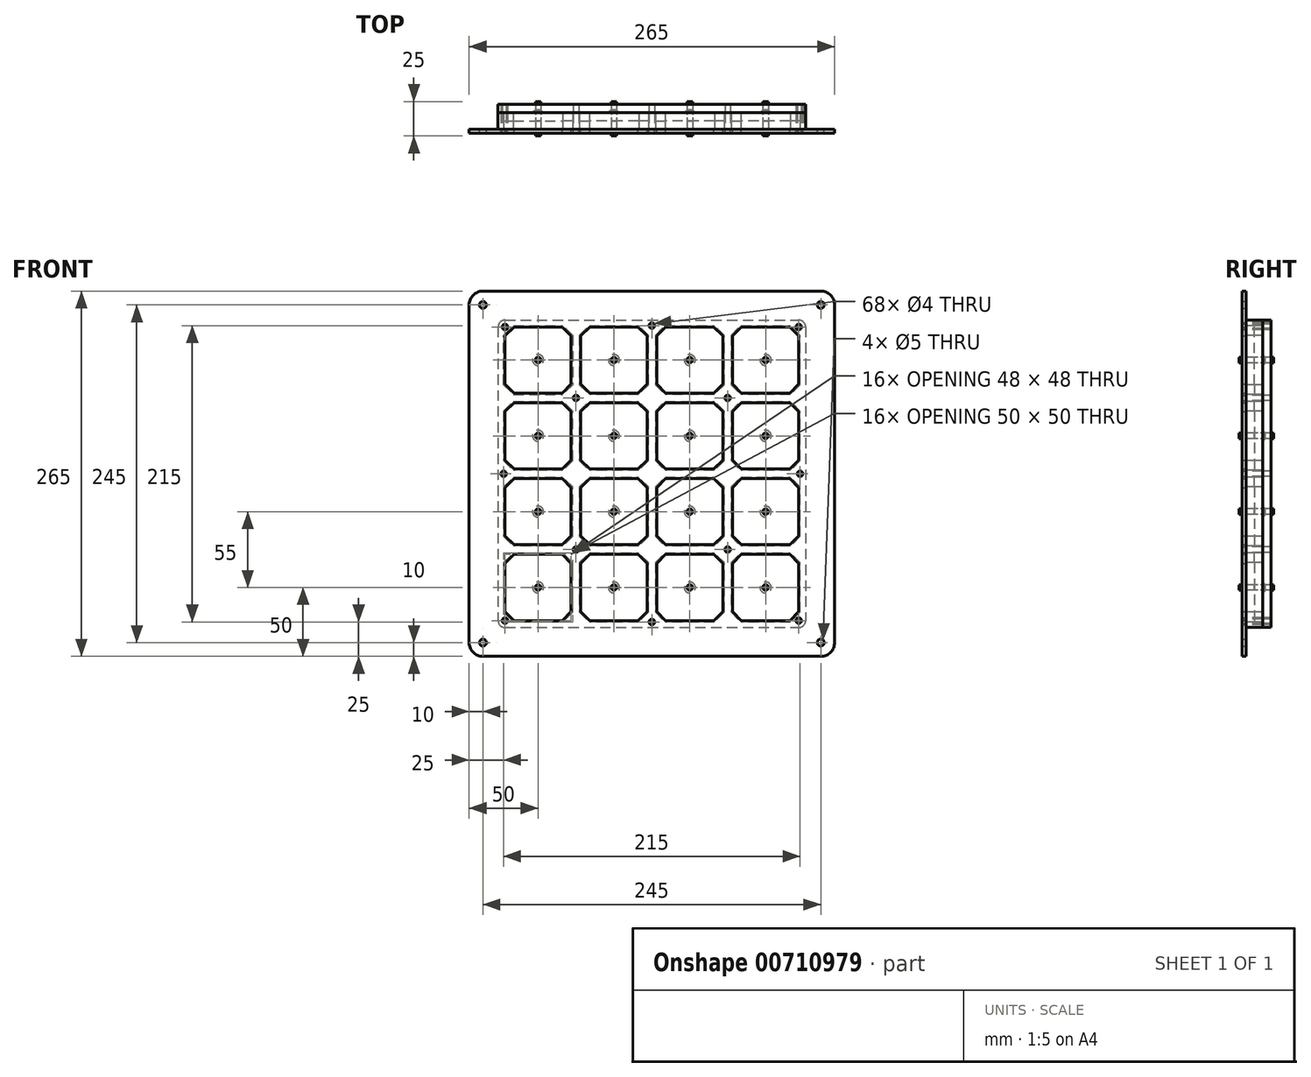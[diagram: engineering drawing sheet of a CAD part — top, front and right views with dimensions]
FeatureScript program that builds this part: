
annotation { "Feature Type Name" : "Feature", "Feature Type Description" : "" }
export const myFeature = defineFeature(function(context is Context, id is Id, definition is map)
    precondition{}
    {
        {
            var Q0;
            Q0=qCreatedBy(makeId("Front.planeOp"),FACE);
            var sketch = newSketch(context, id + "F0", { "sketchPlane" : qUnion([Q0])});
            skLineSegment(sketch, "E0.bottom", {"start": v(-106.5, 111.5) * mm, "end": v(106.5, 111.5) * mm});
            skLineSegment(sketch, "E0.top", {"start": v(-106.5, -111.5) * mm, "end": v(106.5, -111.5) * mm});
            skLineSegment(sketch, "E0.left", {"start": v(-111.5, 106.5) * mm, "end": v(-111.5, -106.5) * mm});
            skLineSegment(sketch, "E0.right", {"start": v(111.5, 106.5) * mm, "end": v(111.5, -106.5) * mm});
            skLineSegment(sketch, "E1", {"start": v(-82.5, 107.5) * mm, "end": v(-82.5, 57.5) * mm, "construction": true});
            skLineSegment(sketch, "E2", {"start": v(-107.5, 82.5) * mm, "end": v(-82.5, 82.5) * mm, "construction": true});
            skLineSegment(sketch, "E3", {"start": v(-82.5, 82.5) * mm, "end": v(-57.5, 82.5) * mm, "construction": true});
            skLineSegment(sketch, "E4", {"start": v(-107.5, 82.5) * mm, "end": v(-107.5, 100.43) * mm});
            skLineSegment(sketch, "E5", {"start": v(-107.5, 100.43) * mm, "end": v(-100.43, 107.5) * mm});
            skLineSegment(sketch, "E6", {"start": v(-100.43, 107.5) * mm, "end": v(-82.5, 107.5) * mm});
            skLineSegment(sketch, "E7.MirrorCS", {"start": v(-57.5, 82.5) * mm, "end": v(-57.5, 100.43) * mm});
            skLineSegment(sketch, "E8.MirrorCS", {"start": v(-57.5, 100.43) * mm, "end": v(-64.57, 107.5) * mm});
            skLineSegment(sketch, "E9.MirrorCS", {"start": v(-64.57, 107.5) * mm, "end": v(-82.5, 107.5) * mm});
            skLineSegment(sketch, "E10.MirrorCS", {"start": v(-57.5, 82.5) * mm, "end": v(-57.5, 64.57) * mm});
            skLineSegment(sketch, "E11.MirrorCS", {"start": v(-57.5, 64.57) * mm, "end": v(-64.57, 57.5) * mm});
            skLineSegment(sketch, "E12.MirrorCS", {"start": v(-64.57, 57.5) * mm, "end": v(-82.5, 57.5) * mm});
            skLineSegment(sketch, "E13.MirrorCS", {"start": v(-100.43, 57.5) * mm, "end": v(-82.5, 57.5) * mm});
            skLineSegment(sketch, "E14.MirrorCS", {"start": v(-107.5, 82.5) * mm, "end": v(-107.5, 64.57) * mm});
            skLineSegment(sketch, "E15.MirrorCS", {"start": v(-107.5, 64.57) * mm, "end": v(-100.43, 57.5) * mm});
            skPoint(sketch, "E16.visualSharp", {"position": v(-111.5, 111.5) * mm});
            skArc(sketch, "E16.filletArc", {"start": v(-106.5, 111.5) * mm, "mid": v(-110.04, 110.04) * mm, "end": v(-111.5, 106.5) * mm});
            skPoint(sketch, "E17.visualSharp", {"position": v(111.5, 111.5) * mm});
            skArc(sketch, "E17.filletArc", {"start": v(111.5, 106.5) * mm, "mid": v(110.04, 110.04) * mm, "end": v(106.5, 111.5) * mm});
            skPoint(sketch, "E18.visualSharp", {"position": v(111.5, -111.5) * mm});
            skArc(sketch, "E18.filletArc", {"start": v(106.5, -111.5) * mm, "mid": v(110.04, -110.04) * mm, "end": v(111.5, -106.5) * mm});
            skPoint(sketch, "E19.visualSharp", {"position": v(-111.5, -111.5) * mm});
            skArc(sketch, "E19.filletArc", {"start": v(-111.5, -106.5) * mm, "mid": v(-110.04, -110.04) * mm, "end": v(-106.5, -111.5) * mm});
            skCircle(sketch, "E20", {"center": v(-82.5, 82.5) * mm, "radius": 2 * mm});
            skLineSegment(sketch, "E21.0.1.0", {"start": v(-57.5, 45.43) * mm, "end": v(-64.57, 52.5) * mm});
            skLineSegment(sketch, "E21.0.1.1", {"start": v(-107.5, 27.5) * mm, "end": v(-82.5, 27.5) * mm, "construction": true});
            skLineSegment(sketch, "E21.0.1.2", {"start": v(-100.43, 52.5) * mm, "end": v(-82.5, 52.5) * mm});
            skLineSegment(sketch, "E21.0.1.3", {"start": v(-107.5, 45.43) * mm, "end": v(-100.43, 52.5) * mm});
            skLineSegment(sketch, "E21.0.1.4", {"start": v(-107.5, 27.5) * mm, "end": v(-107.5, 45.43) * mm});
            skLineSegment(sketch, "E21.0.1.5", {"start": v(-64.57, 52.5) * mm, "end": v(-82.5, 52.5) * mm});
            skLineSegment(sketch, "E21.0.1.6", {"start": v(-107.5, 9.57) * mm, "end": v(-100.43, 2.5) * mm});
            skLineSegment(sketch, "E21.0.1.7", {"start": v(-64.57, 2.5) * mm, "end": v(-82.5, 2.5) * mm});
            skCircle(sketch, "E21.0.1.8", {"center": v(-82.5, 27.5) * mm, "radius": 2 * mm});
            skLineSegment(sketch, "E21.0.1.9", {"start": v(-57.5, 9.57) * mm, "end": v(-64.57, 2.5) * mm});
            skLineSegment(sketch, "E21.0.1.10", {"start": v(-100.43, 2.5) * mm, "end": v(-82.5, 2.5) * mm});
            skLineSegment(sketch, "E21.0.1.11", {"start": v(-82.5, 27.5) * mm, "end": v(-57.5, 27.5) * mm, "construction": true});
            skLineSegment(sketch, "E21.0.1.12", {"start": v(-57.5, 27.5) * mm, "end": v(-57.5, 45.43) * mm});
            skLineSegment(sketch, "E21.0.1.13", {"start": v(-57.5, 27.5) * mm, "end": v(-57.5, 9.57) * mm});
            skLineSegment(sketch, "E21.0.1.14", {"start": v(-107.5, 27.5) * mm, "end": v(-107.5, 9.57) * mm});
            skLineSegment(sketch, "E21.0.1.15", {"start": v(-82.5, 52.5) * mm, "end": v(-82.5, 2.5) * mm, "construction": true});
            skLineSegment(sketch, "E21.0.1.16", {"start": v(-57.5, 27.5) * mm, "end": v(-57.5, 45.43) * mm});
            skLineSegment(sketch, "E21.0.1.17", {"start": v(-57.5, 45.43) * mm, "end": v(-64.57, 52.5) * mm});
            skLineSegment(sketch, "E21.0.1.18", {"start": v(-57.5, 27.5) * mm, "end": v(-57.5, 45.43) * mm});
            skLineSegment(sketch, "E21.0.2.0", {"start": v(-57.5, -9.57) * mm, "end": v(-64.57, -2.5) * mm});
            skLineSegment(sketch, "E21.0.2.1", {"start": v(-107.5, -27.5) * mm, "end": v(-82.5, -27.5) * mm, "construction": true});
            skLineSegment(sketch, "E21.0.2.2", {"start": v(-100.43, -2.5) * mm, "end": v(-82.5, -2.5) * mm});
            skLineSegment(sketch, "E21.0.2.3", {"start": v(-107.5, -9.57) * mm, "end": v(-100.43, -2.5) * mm});
            skLineSegment(sketch, "E21.0.2.4", {"start": v(-107.5, -27.5) * mm, "end": v(-107.5, -9.57) * mm});
            skLineSegment(sketch, "E21.0.2.5", {"start": v(-64.57, -2.5) * mm, "end": v(-82.5, -2.5) * mm});
            skLineSegment(sketch, "E21.0.2.6", {"start": v(-107.5, -45.43) * mm, "end": v(-100.43, -52.5) * mm});
            skLineSegment(sketch, "E21.0.2.7", {"start": v(-64.57, -52.5) * mm, "end": v(-82.5, -52.5) * mm});
            skCircle(sketch, "E21.0.2.8", {"center": v(-82.5, -27.5) * mm, "radius": 2 * mm});
            skLineSegment(sketch, "E21.0.2.9", {"start": v(-57.5, -45.43) * mm, "end": v(-64.57, -52.5) * mm});
            skLineSegment(sketch, "E21.0.2.10", {"start": v(-100.43, -52.5) * mm, "end": v(-82.5, -52.5) * mm});
            skLineSegment(sketch, "E21.0.2.11", {"start": v(-82.5, -27.5) * mm, "end": v(-57.5, -27.5) * mm, "construction": true});
            skLineSegment(sketch, "E21.0.2.12", {"start": v(-57.5, -27.5) * mm, "end": v(-57.5, -9.57) * mm});
            skLineSegment(sketch, "E21.0.2.13", {"start": v(-57.5, -27.5) * mm, "end": v(-57.5, -45.43) * mm});
            skLineSegment(sketch, "E21.0.2.14", {"start": v(-107.5, -27.5) * mm, "end": v(-107.5, -45.43) * mm});
            skLineSegment(sketch, "E21.0.2.15", {"start": v(-82.5, -2.5) * mm, "end": v(-82.5, -52.5) * mm, "construction": true});
            skLineSegment(sketch, "E21.0.2.16", {"start": v(-57.5, -27.5) * mm, "end": v(-57.5, -9.57) * mm});
            skLineSegment(sketch, "E21.0.2.17", {"start": v(-57.5, -9.57) * mm, "end": v(-64.57, -2.5) * mm});
            skLineSegment(sketch, "E21.0.2.18", {"start": v(-57.5, -27.5) * mm, "end": v(-57.5, -9.57) * mm});
            skLineSegment(sketch, "E21.0.3.0", {"start": v(-57.5, -64.57) * mm, "end": v(-64.57, -57.5) * mm});
            skLineSegment(sketch, "E21.0.3.1", {"start": v(-107.5, -82.5) * mm, "end": v(-82.5, -82.5) * mm, "construction": true});
            skLineSegment(sketch, "E21.0.3.2", {"start": v(-100.43, -57.5) * mm, "end": v(-82.5, -57.5) * mm});
            skLineSegment(sketch, "E21.0.3.3", {"start": v(-107.5, -64.57) * mm, "end": v(-100.43, -57.5) * mm});
            skLineSegment(sketch, "E21.0.3.4", {"start": v(-107.5, -82.5) * mm, "end": v(-107.5, -64.57) * mm});
            skLineSegment(sketch, "E21.0.3.5", {"start": v(-64.57, -57.5) * mm, "end": v(-82.5, -57.5) * mm});
            skLineSegment(sketch, "E21.0.3.6", {"start": v(-107.5, -100.43) * mm, "end": v(-100.43, -107.5) * mm});
            skLineSegment(sketch, "E21.0.3.7", {"start": v(-64.57, -107.5) * mm, "end": v(-82.5, -107.5) * mm});
            skCircle(sketch, "E21.0.3.8", {"center": v(-82.5, -82.5) * mm, "radius": 2 * mm});
            skLineSegment(sketch, "E21.0.3.9", {"start": v(-57.5, -100.43) * mm, "end": v(-64.57, -107.5) * mm});
            skLineSegment(sketch, "E21.0.3.10", {"start": v(-100.43, -107.5) * mm, "end": v(-82.5, -107.5) * mm});
            skLineSegment(sketch, "E21.0.3.11", {"start": v(-82.5, -82.5) * mm, "end": v(-57.5, -82.5) * mm, "construction": true});
            skLineSegment(sketch, "E21.0.3.12", {"start": v(-57.5, -82.5) * mm, "end": v(-57.5, -64.57) * mm});
            skLineSegment(sketch, "E21.0.3.13", {"start": v(-57.5, -82.5) * mm, "end": v(-57.5, -100.43) * mm});
            skLineSegment(sketch, "E21.0.3.14", {"start": v(-107.5, -82.5) * mm, "end": v(-107.5, -100.43) * mm});
            skLineSegment(sketch, "E21.0.3.15", {"start": v(-82.5, -57.5) * mm, "end": v(-82.5, -107.5) * mm, "construction": true});
            skLineSegment(sketch, "E21.0.3.16", {"start": v(-57.5, -82.5) * mm, "end": v(-57.5, -64.57) * mm});
            skLineSegment(sketch, "E21.0.3.17", {"start": v(-57.5, -64.57) * mm, "end": v(-64.57, -57.5) * mm});
            skLineSegment(sketch, "E21.0.3.18", {"start": v(-57.5, -82.5) * mm, "end": v(-57.5, -64.57) * mm});
            skLineSegment(sketch, "E21.1.0.0", {"start": v(-2.5, 100.43) * mm, "end": v(-9.57, 107.5) * mm});
            skLineSegment(sketch, "E21.1.0.1", {"start": v(-52.5, 82.5) * mm, "end": v(-27.5, 82.5) * mm, "construction": true});
            skLineSegment(sketch, "E21.1.0.2", {"start": v(-45.43, 107.5) * mm, "end": v(-27.5, 107.5) * mm});
            skLineSegment(sketch, "E21.1.0.3", {"start": v(-52.5, 100.43) * mm, "end": v(-45.43, 107.5) * mm});
            skLineSegment(sketch, "E21.1.0.4", {"start": v(-52.5, 82.5) * mm, "end": v(-52.5, 100.43) * mm});
            skLineSegment(sketch, "E21.1.0.5", {"start": v(-9.57, 107.5) * mm, "end": v(-27.5, 107.5) * mm});
            skLineSegment(sketch, "E21.1.0.6", {"start": v(-52.5, 64.57) * mm, "end": v(-45.43, 57.5) * mm});
            skLineSegment(sketch, "E21.1.0.7", {"start": v(-9.57, 57.5) * mm, "end": v(-27.5, 57.5) * mm});
            skCircle(sketch, "E21.1.0.8", {"center": v(-27.5, 82.5) * mm, "radius": 2 * mm});
            skLineSegment(sketch, "E21.1.0.9", {"start": v(-2.5, 64.57) * mm, "end": v(-9.57, 57.5) * mm});
            skLineSegment(sketch, "E21.1.0.10", {"start": v(-45.43, 57.5) * mm, "end": v(-27.5, 57.5) * mm});
            skLineSegment(sketch, "E21.1.0.11", {"start": v(-27.5, 82.5) * mm, "end": v(-2.5, 82.5) * mm, "construction": true});
            skLineSegment(sketch, "E21.1.0.12", {"start": v(-2.5, 82.5) * mm, "end": v(-2.5, 100.43) * mm});
            skLineSegment(sketch, "E21.1.0.13", {"start": v(-2.5, 82.5) * mm, "end": v(-2.5, 64.57) * mm});
            skLineSegment(sketch, "E21.1.0.14", {"start": v(-52.5, 82.5) * mm, "end": v(-52.5, 64.57) * mm});
            skLineSegment(sketch, "E21.1.0.15", {"start": v(-27.5, 107.5) * mm, "end": v(-27.5, 57.5) * mm, "construction": true});
            skLineSegment(sketch, "E21.1.0.16", {"start": v(-2.5, 82.5) * mm, "end": v(-2.5, 100.43) * mm});
            skLineSegment(sketch, "E21.1.0.17", {"start": v(-2.5, 100.43) * mm, "end": v(-9.57, 107.5) * mm});
            skLineSegment(sketch, "E21.1.0.18", {"start": v(-2.5, 82.5) * mm, "end": v(-2.5, 100.43) * mm});
            skLineSegment(sketch, "E21.1.1.0", {"start": v(-2.5, 45.43) * mm, "end": v(-9.57, 52.5) * mm});
            skLineSegment(sketch, "E21.1.1.1", {"start": v(-52.5, 27.5) * mm, "end": v(-27.5, 27.5) * mm, "construction": true});
            skLineSegment(sketch, "E21.1.1.2", {"start": v(-45.43, 52.5) * mm, "end": v(-27.5, 52.5) * mm});
            skLineSegment(sketch, "E21.1.1.3", {"start": v(-52.5, 45.43) * mm, "end": v(-45.43, 52.5) * mm});
            skLineSegment(sketch, "E21.1.1.4", {"start": v(-52.5, 27.5) * mm, "end": v(-52.5, 45.43) * mm});
            skLineSegment(sketch, "E21.1.1.5", {"start": v(-9.57, 52.5) * mm, "end": v(-27.5, 52.5) * mm});
            skLineSegment(sketch, "E21.1.1.6", {"start": v(-52.5, 9.57) * mm, "end": v(-45.43, 2.5) * mm});
            skLineSegment(sketch, "E21.1.1.7", {"start": v(-9.57, 2.5) * mm, "end": v(-27.5, 2.5) * mm});
            skCircle(sketch, "E21.1.1.8", {"center": v(-27.5, 27.5) * mm, "radius": 2 * mm});
            skLineSegment(sketch, "E21.1.1.9", {"start": v(-2.5, 9.57) * mm, "end": v(-9.57, 2.5) * mm});
            skLineSegment(sketch, "E21.1.1.10", {"start": v(-45.43, 2.5) * mm, "end": v(-27.5, 2.5) * mm});
            skLineSegment(sketch, "E21.1.1.11", {"start": v(-27.5, 27.5) * mm, "end": v(-2.5, 27.5) * mm, "construction": true});
            skLineSegment(sketch, "E21.1.1.12", {"start": v(-2.5, 27.5) * mm, "end": v(-2.5, 45.43) * mm});
            skLineSegment(sketch, "E21.1.1.13", {"start": v(-2.5, 27.5) * mm, "end": v(-2.5, 9.57) * mm});
            skLineSegment(sketch, "E21.1.1.14", {"start": v(-52.5, 27.5) * mm, "end": v(-52.5, 9.57) * mm});
            skLineSegment(sketch, "E21.1.1.15", {"start": v(-27.5, 52.5) * mm, "end": v(-27.5, 2.5) * mm, "construction": true});
            skLineSegment(sketch, "E21.1.1.16", {"start": v(-2.5, 27.5) * mm, "end": v(-2.5, 45.43) * mm});
            skLineSegment(sketch, "E21.1.1.17", {"start": v(-2.5, 45.43) * mm, "end": v(-9.57, 52.5) * mm});
            skLineSegment(sketch, "E21.1.1.18", {"start": v(-2.5, 27.5) * mm, "end": v(-2.5, 45.43) * mm});
            skLineSegment(sketch, "E21.1.2.0", {"start": v(-2.5, -9.57) * mm, "end": v(-9.57, -2.5) * mm});
            skLineSegment(sketch, "E21.1.2.1", {"start": v(-52.5, -27.5) * mm, "end": v(-27.5, -27.5) * mm, "construction": true});
            skLineSegment(sketch, "E21.1.2.2", {"start": v(-45.43, -2.5) * mm, "end": v(-27.5, -2.5) * mm});
            skLineSegment(sketch, "E21.1.2.3", {"start": v(-52.5, -9.57) * mm, "end": v(-45.43, -2.5) * mm});
            skLineSegment(sketch, "E21.1.2.4", {"start": v(-52.5, -27.5) * mm, "end": v(-52.5, -9.57) * mm});
            skLineSegment(sketch, "E21.1.2.5", {"start": v(-9.57, -2.5) * mm, "end": v(-27.5, -2.5) * mm});
            skLineSegment(sketch, "E21.1.2.6", {"start": v(-52.5, -45.43) * mm, "end": v(-45.43, -52.5) * mm});
            skLineSegment(sketch, "E21.1.2.7", {"start": v(-9.57, -52.5) * mm, "end": v(-27.5, -52.5) * mm});
            skCircle(sketch, "E21.1.2.8", {"center": v(-27.5, -27.5) * mm, "radius": 2 * mm});
            skLineSegment(sketch, "E21.1.2.9", {"start": v(-2.5, -45.43) * mm, "end": v(-9.57, -52.5) * mm});
            skLineSegment(sketch, "E21.1.2.10", {"start": v(-45.43, -52.5) * mm, "end": v(-27.5, -52.5) * mm});
            skLineSegment(sketch, "E21.1.2.11", {"start": v(-27.5, -27.5) * mm, "end": v(-2.5, -27.5) * mm, "construction": true});
            skLineSegment(sketch, "E21.1.2.12", {"start": v(-2.5, -27.5) * mm, "end": v(-2.5, -9.57) * mm});
            skLineSegment(sketch, "E21.1.2.13", {"start": v(-2.5, -27.5) * mm, "end": v(-2.5, -45.43) * mm});
            skLineSegment(sketch, "E21.1.2.14", {"start": v(-52.5, -27.5) * mm, "end": v(-52.5, -45.43) * mm});
            skLineSegment(sketch, "E21.1.2.15", {"start": v(-27.5, -2.5) * mm, "end": v(-27.5, -52.5) * mm, "construction": true});
            skLineSegment(sketch, "E21.1.2.16", {"start": v(-2.5, -27.5) * mm, "end": v(-2.5, -9.57) * mm});
            skLineSegment(sketch, "E21.1.2.17", {"start": v(-2.5, -9.57) * mm, "end": v(-9.57, -2.5) * mm});
            skLineSegment(sketch, "E21.1.2.18", {"start": v(-2.5, -27.5) * mm, "end": v(-2.5, -9.57) * mm});
            skLineSegment(sketch, "E21.1.3.0", {"start": v(-2.5, -64.57) * mm, "end": v(-9.57, -57.5) * mm});
            skLineSegment(sketch, "E21.1.3.1", {"start": v(-52.5, -82.5) * mm, "end": v(-27.5, -82.5) * mm, "construction": true});
            skLineSegment(sketch, "E21.1.3.2", {"start": v(-45.43, -57.5) * mm, "end": v(-27.5, -57.5) * mm});
            skLineSegment(sketch, "E21.1.3.3", {"start": v(-52.5, -64.57) * mm, "end": v(-45.43, -57.5) * mm});
            skLineSegment(sketch, "E21.1.3.4", {"start": v(-52.5, -82.5) * mm, "end": v(-52.5, -64.57) * mm});
            skLineSegment(sketch, "E21.1.3.5", {"start": v(-9.57, -57.5) * mm, "end": v(-27.5, -57.5) * mm});
            skLineSegment(sketch, "E21.1.3.6", {"start": v(-52.5, -100.43) * mm, "end": v(-45.43, -107.5) * mm});
            skLineSegment(sketch, "E21.1.3.7", {"start": v(-9.57, -107.5) * mm, "end": v(-27.5, -107.5) * mm});
            skCircle(sketch, "E21.1.3.8", {"center": v(-27.5, -82.5) * mm, "radius": 2 * mm});
            skLineSegment(sketch, "E21.1.3.9", {"start": v(-2.5, -100.43) * mm, "end": v(-9.57, -107.5) * mm});
            skLineSegment(sketch, "E21.1.3.10", {"start": v(-45.43, -107.5) * mm, "end": v(-27.5, -107.5) * mm});
            skLineSegment(sketch, "E21.1.3.11", {"start": v(-27.5, -82.5) * mm, "end": v(-2.5, -82.5) * mm, "construction": true});
            skLineSegment(sketch, "E21.1.3.12", {"start": v(-2.5, -82.5) * mm, "end": v(-2.5, -64.57) * mm});
            skLineSegment(sketch, "E21.1.3.13", {"start": v(-2.5, -82.5) * mm, "end": v(-2.5, -100.43) * mm});
            skLineSegment(sketch, "E21.1.3.14", {"start": v(-52.5, -82.5) * mm, "end": v(-52.5, -100.43) * mm});
            skLineSegment(sketch, "E21.1.3.15", {"start": v(-27.5, -57.5) * mm, "end": v(-27.5, -107.5) * mm, "construction": true});
            skLineSegment(sketch, "E21.1.3.16", {"start": v(-2.5, -82.5) * mm, "end": v(-2.5, -64.57) * mm});
            skLineSegment(sketch, "E21.1.3.17", {"start": v(-2.5, -64.57) * mm, "end": v(-9.57, -57.5) * mm});
            skLineSegment(sketch, "E21.1.3.18", {"start": v(-2.5, -82.5) * mm, "end": v(-2.5, -64.57) * mm});
            skLineSegment(sketch, "E21.2.0.0", {"start": v(52.5, 100.43) * mm, "end": v(45.43, 107.5) * mm});
            skLineSegment(sketch, "E21.2.0.1", {"start": v(2.5, 82.5) * mm, "end": v(27.5, 82.5) * mm, "construction": true});
            skLineSegment(sketch, "E21.2.0.2", {"start": v(9.57, 107.5) * mm, "end": v(27.5, 107.5) * mm});
            skLineSegment(sketch, "E21.2.0.3", {"start": v(2.5, 100.43) * mm, "end": v(9.57, 107.5) * mm});
            skLineSegment(sketch, "E21.2.0.4", {"start": v(2.5, 82.5) * mm, "end": v(2.5, 100.43) * mm});
            skLineSegment(sketch, "E21.2.0.5", {"start": v(45.43, 107.5) * mm, "end": v(27.5, 107.5) * mm});
            skLineSegment(sketch, "E21.2.0.6", {"start": v(2.5, 64.57) * mm, "end": v(9.57, 57.5) * mm});
            skLineSegment(sketch, "E21.2.0.7", {"start": v(45.43, 57.5) * mm, "end": v(27.5, 57.5) * mm});
            skCircle(sketch, "E21.2.0.8", {"center": v(27.5, 82.5) * mm, "radius": 2 * mm});
            skLineSegment(sketch, "E21.2.0.9", {"start": v(52.5, 64.57) * mm, "end": v(45.43, 57.5) * mm});
            skLineSegment(sketch, "E21.2.0.10", {"start": v(9.57, 57.5) * mm, "end": v(27.5, 57.5) * mm});
            skLineSegment(sketch, "E21.2.0.11", {"start": v(27.5, 82.5) * mm, "end": v(52.5, 82.5) * mm, "construction": true});
            skLineSegment(sketch, "E21.2.0.12", {"start": v(52.5, 82.5) * mm, "end": v(52.5, 100.43) * mm});
            skLineSegment(sketch, "E21.2.0.13", {"start": v(52.5, 82.5) * mm, "end": v(52.5, 64.57) * mm});
            skLineSegment(sketch, "E21.2.0.14", {"start": v(2.5, 82.5) * mm, "end": v(2.5, 64.57) * mm});
            skLineSegment(sketch, "E21.2.0.15", {"start": v(27.5, 107.5) * mm, "end": v(27.5, 57.5) * mm, "construction": true});
            skLineSegment(sketch, "E21.2.0.16", {"start": v(52.5, 82.5) * mm, "end": v(52.5, 100.43) * mm});
            skLineSegment(sketch, "E21.2.0.17", {"start": v(52.5, 100.43) * mm, "end": v(45.43, 107.5) * mm});
            skLineSegment(sketch, "E21.2.0.18", {"start": v(52.5, 82.5) * mm, "end": v(52.5, 100.43) * mm});
            skLineSegment(sketch, "E21.2.1.0", {"start": v(52.5, 45.43) * mm, "end": v(45.43, 52.5) * mm});
            skLineSegment(sketch, "E21.2.1.1", {"start": v(2.5, 27.5) * mm, "end": v(27.5, 27.5) * mm, "construction": true});
            skLineSegment(sketch, "E21.2.1.2", {"start": v(9.57, 52.5) * mm, "end": v(27.5, 52.5) * mm});
            skLineSegment(sketch, "E21.2.1.3", {"start": v(2.5, 45.43) * mm, "end": v(9.57, 52.5) * mm});
            skLineSegment(sketch, "E21.2.1.4", {"start": v(2.5, 27.5) * mm, "end": v(2.5, 45.43) * mm});
            skLineSegment(sketch, "E21.2.1.5", {"start": v(45.43, 52.5) * mm, "end": v(27.5, 52.5) * mm});
            skLineSegment(sketch, "E21.2.1.6", {"start": v(2.5, 9.57) * mm, "end": v(9.57, 2.5) * mm});
            skLineSegment(sketch, "E21.2.1.7", {"start": v(45.43, 2.5) * mm, "end": v(27.5, 2.5) * mm});
            skCircle(sketch, "E21.2.1.8", {"center": v(27.5, 27.5) * mm, "radius": 2 * mm});
            skLineSegment(sketch, "E21.2.1.9", {"start": v(52.5, 9.57) * mm, "end": v(45.43, 2.5) * mm});
            skLineSegment(sketch, "E21.2.1.10", {"start": v(9.57, 2.5) * mm, "end": v(27.5, 2.5) * mm});
            skLineSegment(sketch, "E21.2.1.11", {"start": v(27.5, 27.5) * mm, "end": v(52.5, 27.5) * mm, "construction": true});
            skLineSegment(sketch, "E21.2.1.12", {"start": v(52.5, 27.5) * mm, "end": v(52.5, 45.43) * mm});
            skLineSegment(sketch, "E21.2.1.13", {"start": v(52.5, 27.5) * mm, "end": v(52.5, 9.57) * mm});
            skLineSegment(sketch, "E21.2.1.14", {"start": v(2.5, 27.5) * mm, "end": v(2.5, 9.57) * mm});
            skLineSegment(sketch, "E21.2.1.15", {"start": v(27.5, 52.5) * mm, "end": v(27.5, 2.5) * mm, "construction": true});
            skLineSegment(sketch, "E21.2.1.16", {"start": v(52.5, 27.5) * mm, "end": v(52.5, 45.43) * mm});
            skLineSegment(sketch, "E21.2.1.17", {"start": v(52.5, 45.43) * mm, "end": v(45.43, 52.5) * mm});
            skLineSegment(sketch, "E21.2.1.18", {"start": v(52.5, 27.5) * mm, "end": v(52.5, 45.43) * mm});
            skLineSegment(sketch, "E21.2.2.0", {"start": v(52.5, -9.57) * mm, "end": v(45.43, -2.5) * mm});
            skLineSegment(sketch, "E21.2.2.1", {"start": v(2.5, -27.5) * mm, "end": v(27.5, -27.5) * mm, "construction": true});
            skLineSegment(sketch, "E21.2.2.2", {"start": v(9.57, -2.5) * mm, "end": v(27.5, -2.5) * mm});
            skLineSegment(sketch, "E21.2.2.3", {"start": v(2.5, -9.57) * mm, "end": v(9.57, -2.5) * mm});
            skLineSegment(sketch, "E21.2.2.4", {"start": v(2.5, -27.5) * mm, "end": v(2.5, -9.57) * mm});
            skLineSegment(sketch, "E21.2.2.5", {"start": v(45.43, -2.5) * mm, "end": v(27.5, -2.5) * mm});
            skLineSegment(sketch, "E21.2.2.6", {"start": v(2.5, -45.43) * mm, "end": v(9.57, -52.5) * mm});
            skLineSegment(sketch, "E21.2.2.7", {"start": v(45.43, -52.5) * mm, "end": v(27.5, -52.5) * mm});
            skCircle(sketch, "E21.2.2.8", {"center": v(27.5, -27.5) * mm, "radius": 2 * mm});
            skLineSegment(sketch, "E21.2.2.9", {"start": v(52.5, -45.43) * mm, "end": v(45.43, -52.5) * mm});
            skLineSegment(sketch, "E21.2.2.10", {"start": v(9.57, -52.5) * mm, "end": v(27.5, -52.5) * mm});
            skLineSegment(sketch, "E21.2.2.11", {"start": v(27.5, -27.5) * mm, "end": v(52.5, -27.5) * mm, "construction": true});
            skLineSegment(sketch, "E21.2.2.12", {"start": v(52.5, -27.5) * mm, "end": v(52.5, -9.57) * mm});
            skLineSegment(sketch, "E21.2.2.13", {"start": v(52.5, -27.5) * mm, "end": v(52.5, -45.43) * mm});
            skLineSegment(sketch, "E21.2.2.14", {"start": v(2.5, -27.5) * mm, "end": v(2.5, -45.43) * mm});
            skLineSegment(sketch, "E21.2.2.15", {"start": v(27.5, -2.5) * mm, "end": v(27.5, -52.5) * mm, "construction": true});
            skLineSegment(sketch, "E21.2.2.16", {"start": v(52.5, -27.5) * mm, "end": v(52.5, -9.57) * mm});
            skLineSegment(sketch, "E21.2.2.17", {"start": v(52.5, -9.57) * mm, "end": v(45.43, -2.5) * mm});
            skLineSegment(sketch, "E21.2.2.18", {"start": v(52.5, -27.5) * mm, "end": v(52.5, -9.57) * mm});
            skLineSegment(sketch, "E21.2.3.0", {"start": v(52.5, -64.57) * mm, "end": v(45.43, -57.5) * mm});
            skLineSegment(sketch, "E21.2.3.1", {"start": v(2.5, -82.5) * mm, "end": v(27.5, -82.5) * mm, "construction": true});
            skLineSegment(sketch, "E21.2.3.2", {"start": v(9.57, -57.5) * mm, "end": v(27.5, -57.5) * mm});
            skLineSegment(sketch, "E21.2.3.3", {"start": v(2.5, -64.57) * mm, "end": v(9.57, -57.5) * mm});
            skLineSegment(sketch, "E21.2.3.4", {"start": v(2.5, -82.5) * mm, "end": v(2.5, -64.57) * mm});
            skLineSegment(sketch, "E21.2.3.5", {"start": v(45.43, -57.5) * mm, "end": v(27.5, -57.5) * mm});
            skLineSegment(sketch, "E21.2.3.6", {"start": v(2.5, -100.43) * mm, "end": v(9.57, -107.5) * mm});
            skLineSegment(sketch, "E21.2.3.7", {"start": v(45.43, -107.5) * mm, "end": v(27.5, -107.5) * mm});
            skCircle(sketch, "E21.2.3.8", {"center": v(27.5, -82.5) * mm, "radius": 2 * mm});
            skLineSegment(sketch, "E21.2.3.9", {"start": v(52.5, -100.43) * mm, "end": v(45.43, -107.5) * mm});
            skLineSegment(sketch, "E21.2.3.10", {"start": v(9.57, -107.5) * mm, "end": v(27.5, -107.5) * mm});
            skLineSegment(sketch, "E21.2.3.11", {"start": v(27.5, -82.5) * mm, "end": v(52.5, -82.5) * mm, "construction": true});
            skLineSegment(sketch, "E21.2.3.12", {"start": v(52.5, -82.5) * mm, "end": v(52.5, -64.57) * mm});
            skLineSegment(sketch, "E21.2.3.13", {"start": v(52.5, -82.5) * mm, "end": v(52.5, -100.43) * mm});
            skLineSegment(sketch, "E21.2.3.14", {"start": v(2.5, -82.5) * mm, "end": v(2.5, -100.43) * mm});
            skLineSegment(sketch, "E21.2.3.15", {"start": v(27.5, -57.5) * mm, "end": v(27.5, -107.5) * mm, "construction": true});
            skLineSegment(sketch, "E21.2.3.16", {"start": v(52.5, -82.5) * mm, "end": v(52.5, -64.57) * mm});
            skLineSegment(sketch, "E21.2.3.17", {"start": v(52.5, -64.57) * mm, "end": v(45.43, -57.5) * mm});
            skLineSegment(sketch, "E21.2.3.18", {"start": v(52.5, -82.5) * mm, "end": v(52.5, -64.57) * mm});
            skLineSegment(sketch, "E21.3.0.0", {"start": v(107.5, 100.43) * mm, "end": v(100.43, 107.5) * mm});
            skLineSegment(sketch, "E21.3.0.1", {"start": v(57.5, 82.5) * mm, "end": v(82.5, 82.5) * mm, "construction": true});
            skLineSegment(sketch, "E21.3.0.2", {"start": v(64.57, 107.5) * mm, "end": v(82.5, 107.5) * mm});
            skLineSegment(sketch, "E21.3.0.3", {"start": v(57.5, 100.43) * mm, "end": v(64.57, 107.5) * mm});
            skLineSegment(sketch, "E21.3.0.4", {"start": v(57.5, 82.5) * mm, "end": v(57.5, 100.43) * mm});
            skLineSegment(sketch, "E21.3.0.5", {"start": v(100.43, 107.5) * mm, "end": v(82.5, 107.5) * mm});
            skLineSegment(sketch, "E21.3.0.6", {"start": v(57.5, 64.57) * mm, "end": v(64.57, 57.5) * mm});
            skLineSegment(sketch, "E21.3.0.7", {"start": v(100.43, 57.5) * mm, "end": v(82.5, 57.5) * mm});
            skCircle(sketch, "E21.3.0.8", {"center": v(82.5, 82.5) * mm, "radius": 2 * mm});
            skLineSegment(sketch, "E21.3.0.9", {"start": v(107.5, 64.57) * mm, "end": v(100.43, 57.5) * mm});
            skLineSegment(sketch, "E21.3.0.10", {"start": v(64.57, 57.5) * mm, "end": v(82.5, 57.5) * mm});
            skLineSegment(sketch, "E21.3.0.11", {"start": v(82.5, 82.5) * mm, "end": v(107.5, 82.5) * mm, "construction": true});
            skLineSegment(sketch, "E21.3.0.12", {"start": v(107.5, 82.5) * mm, "end": v(107.5, 100.43) * mm});
            skLineSegment(sketch, "E21.3.0.13", {"start": v(107.5, 82.5) * mm, "end": v(107.5, 64.57) * mm});
            skLineSegment(sketch, "E21.3.0.14", {"start": v(57.5, 82.5) * mm, "end": v(57.5, 64.57) * mm});
            skLineSegment(sketch, "E21.3.0.15", {"start": v(82.5, 107.5) * mm, "end": v(82.5, 57.5) * mm, "construction": true});
            skLineSegment(sketch, "E21.3.0.16", {"start": v(107.5, 82.5) * mm, "end": v(107.5, 100.43) * mm});
            skLineSegment(sketch, "E21.3.0.17", {"start": v(107.5, 100.43) * mm, "end": v(100.43, 107.5) * mm});
            skLineSegment(sketch, "E21.3.0.18", {"start": v(107.5, 82.5) * mm, "end": v(107.5, 100.43) * mm});
            skLineSegment(sketch, "E21.3.1.0", {"start": v(107.5, 45.43) * mm, "end": v(100.43, 52.5) * mm});
            skLineSegment(sketch, "E21.3.1.1", {"start": v(57.5, 27.5) * mm, "end": v(82.5, 27.5) * mm, "construction": true});
            skLineSegment(sketch, "E21.3.1.2", {"start": v(64.57, 52.5) * mm, "end": v(82.5, 52.5) * mm});
            skLineSegment(sketch, "E21.3.1.3", {"start": v(57.5, 45.43) * mm, "end": v(64.57, 52.5) * mm});
            skLineSegment(sketch, "E21.3.1.4", {"start": v(57.5, 27.5) * mm, "end": v(57.5, 45.43) * mm});
            skLineSegment(sketch, "E21.3.1.5", {"start": v(100.43, 52.5) * mm, "end": v(82.5, 52.5) * mm});
            skLineSegment(sketch, "E21.3.1.6", {"start": v(57.5, 9.57) * mm, "end": v(64.57, 2.5) * mm});
            skLineSegment(sketch, "E21.3.1.7", {"start": v(100.43, 2.5) * mm, "end": v(82.5, 2.5) * mm});
            skCircle(sketch, "E21.3.1.8", {"center": v(82.5, 27.5) * mm, "radius": 2 * mm});
            skLineSegment(sketch, "E21.3.1.9", {"start": v(107.5, 9.57) * mm, "end": v(100.43, 2.5) * mm});
            skLineSegment(sketch, "E21.3.1.10", {"start": v(64.57, 2.5) * mm, "end": v(82.5, 2.5) * mm});
            skLineSegment(sketch, "E21.3.1.11", {"start": v(82.5, 27.5) * mm, "end": v(107.5, 27.5) * mm, "construction": true});
            skLineSegment(sketch, "E21.3.1.12", {"start": v(107.5, 27.5) * mm, "end": v(107.5, 45.43) * mm});
            skLineSegment(sketch, "E21.3.1.13", {"start": v(107.5, 27.5) * mm, "end": v(107.5, 9.57) * mm});
            skLineSegment(sketch, "E21.3.1.14", {"start": v(57.5, 27.5) * mm, "end": v(57.5, 9.57) * mm});
            skLineSegment(sketch, "E21.3.1.15", {"start": v(82.5, 52.5) * mm, "end": v(82.5, 2.5) * mm, "construction": true});
            skLineSegment(sketch, "E21.3.1.16", {"start": v(107.5, 27.5) * mm, "end": v(107.5, 45.43) * mm});
            skLineSegment(sketch, "E21.3.1.17", {"start": v(107.5, 45.43) * mm, "end": v(100.43, 52.5) * mm});
            skLineSegment(sketch, "E21.3.1.18", {"start": v(107.5, 27.5) * mm, "end": v(107.5, 45.43) * mm});
            skLineSegment(sketch, "E21.3.2.0", {"start": v(107.5, -9.57) * mm, "end": v(100.43, -2.5) * mm});
            skLineSegment(sketch, "E21.3.2.1", {"start": v(57.5, -27.5) * mm, "end": v(82.5, -27.5) * mm, "construction": true});
            skLineSegment(sketch, "E21.3.2.2", {"start": v(64.57, -2.5) * mm, "end": v(82.5, -2.5) * mm});
            skLineSegment(sketch, "E21.3.2.3", {"start": v(57.5, -9.57) * mm, "end": v(64.57, -2.5) * mm});
            skLineSegment(sketch, "E21.3.2.4", {"start": v(57.5, -27.5) * mm, "end": v(57.5, -9.57) * mm});
            skLineSegment(sketch, "E21.3.2.5", {"start": v(100.43, -2.5) * mm, "end": v(82.5, -2.5) * mm});
            skLineSegment(sketch, "E21.3.2.6", {"start": v(57.5, -45.43) * mm, "end": v(64.57, -52.5) * mm});
            skLineSegment(sketch, "E21.3.2.7", {"start": v(100.43, -52.5) * mm, "end": v(82.5, -52.5) * mm});
            skCircle(sketch, "E21.3.2.8", {"center": v(82.5, -27.5) * mm, "radius": 2 * mm});
            skLineSegment(sketch, "E21.3.2.9", {"start": v(107.5, -45.43) * mm, "end": v(100.43, -52.5) * mm});
            skLineSegment(sketch, "E21.3.2.10", {"start": v(64.57, -52.5) * mm, "end": v(82.5, -52.5) * mm});
            skLineSegment(sketch, "E21.3.2.11", {"start": v(82.5, -27.5) * mm, "end": v(107.5, -27.5) * mm, "construction": true});
            skLineSegment(sketch, "E21.3.2.12", {"start": v(107.5, -27.5) * mm, "end": v(107.5, -9.57) * mm});
            skLineSegment(sketch, "E21.3.2.13", {"start": v(107.5, -27.5) * mm, "end": v(107.5, -45.43) * mm});
            skLineSegment(sketch, "E21.3.2.14", {"start": v(57.5, -27.5) * mm, "end": v(57.5, -45.43) * mm});
            skLineSegment(sketch, "E21.3.2.15", {"start": v(82.5, -2.5) * mm, "end": v(82.5, -52.5) * mm, "construction": true});
            skLineSegment(sketch, "E21.3.2.16", {"start": v(107.5, -27.5) * mm, "end": v(107.5, -9.57) * mm});
            skLineSegment(sketch, "E21.3.2.17", {"start": v(107.5, -9.57) * mm, "end": v(100.43, -2.5) * mm});
            skLineSegment(sketch, "E21.3.2.18", {"start": v(107.5, -27.5) * mm, "end": v(107.5, -9.57) * mm});
            skLineSegment(sketch, "E21.3.3.0", {"start": v(107.5, -64.57) * mm, "end": v(100.43, -57.5) * mm});
            skLineSegment(sketch, "E21.3.3.1", {"start": v(57.5, -82.5) * mm, "end": v(82.5, -82.5) * mm, "construction": true});
            skLineSegment(sketch, "E21.3.3.2", {"start": v(64.57, -57.5) * mm, "end": v(82.5, -57.5) * mm});
            skLineSegment(sketch, "E21.3.3.3", {"start": v(57.5, -64.57) * mm, "end": v(64.57, -57.5) * mm});
            skLineSegment(sketch, "E21.3.3.4", {"start": v(57.5, -82.5) * mm, "end": v(57.5, -64.57) * mm});
            skLineSegment(sketch, "E21.3.3.5", {"start": v(100.43, -57.5) * mm, "end": v(82.5, -57.5) * mm});
            skLineSegment(sketch, "E21.3.3.6", {"start": v(57.5, -100.43) * mm, "end": v(64.57, -107.5) * mm});
            skLineSegment(sketch, "E21.3.3.7", {"start": v(100.43, -107.5) * mm, "end": v(82.5, -107.5) * mm});
            skCircle(sketch, "E21.3.3.8", {"center": v(82.5, -82.5) * mm, "radius": 2 * mm});
            skLineSegment(sketch, "E21.3.3.9", {"start": v(107.5, -100.43) * mm, "end": v(100.43, -107.5) * mm});
            skLineSegment(sketch, "E21.3.3.10", {"start": v(64.57, -107.5) * mm, "end": v(82.5, -107.5) * mm});
            skLineSegment(sketch, "E21.3.3.11", {"start": v(82.5, -82.5) * mm, "end": v(107.5, -82.5) * mm, "construction": true});
            skLineSegment(sketch, "E21.3.3.12", {"start": v(107.5, -82.5) * mm, "end": v(107.5, -64.57) * mm});
            skLineSegment(sketch, "E21.3.3.13", {"start": v(107.5, -82.5) * mm, "end": v(107.5, -100.43) * mm});
            skLineSegment(sketch, "E21.3.3.14", {"start": v(57.5, -82.5) * mm, "end": v(57.5, -100.43) * mm});
            skLineSegment(sketch, "E21.3.3.15", {"start": v(82.5, -57.5) * mm, "end": v(82.5, -107.5) * mm, "construction": true});
            skLineSegment(sketch, "E21.3.3.16", {"start": v(107.5, -82.5) * mm, "end": v(107.5, -64.57) * mm});
            skLineSegment(sketch, "E21.3.3.17", {"start": v(107.5, -64.57) * mm, "end": v(100.43, -57.5) * mm});
            skLineSegment(sketch, "E21.3.3.18", {"start": v(107.5, -82.5) * mm, "end": v(107.5, -64.57) * mm});
            skLineSegment(sketch, "E21.direction1", {"start": v(-100.43, 57.5) * mm, "end": v(-45.43, 57.5) * mm, "construction": true});
            skLineSegment(sketch, "E21.direction2", {"start": v(-100.43, 57.5) * mm, "end": v(-100.43, 2.5) * mm, "construction": true});
            skLineSegment(sketch, "E22", {"start": v(48.96, 61.04) * mm, "end": v(61.04, 48.96) * mm, "construction": true});
            skLineSegment(sketch, "E23", {"start": v(61.04, 48.96) * mm, "end": v(48.96, 48.96) * mm, "construction": true});
            skLineSegment(sketch, "E24", {"start": v(48.96, 48.96) * mm, "end": v(61.04, 61.04) * mm, "construction": true});
            skLineSegment(sketch, "E25", {"start": v(61.04, -48.96) * mm, "end": v(48.96, -61.04) * mm, "construction": true});
            skLineSegment(sketch, "E26", {"start": v(48.96, -61.04) * mm, "end": v(61.04, -61.04) * mm, "construction": true});
            skLineSegment(sketch, "E27", {"start": v(61.04, -61.04) * mm, "end": v(48.96, -48.96) * mm, "construction": true});
            skLineSegment(sketch, "E28", {"start": v(-48.96, -61.04) * mm, "end": v(-61.04, -48.96) * mm, "construction": true});
            skLineSegment(sketch, "E29", {"start": v(-48.96, -48.96) * mm, "end": v(-61.04, -61.04) * mm, "construction": true});
            skLineSegment(sketch, "E30", {"start": v(-61.04, 61.04) * mm, "end": v(-48.96, 48.96) * mm, "construction": true});
            skLineSegment(sketch, "E31", {"start": v(-48.96, 48.96) * mm, "end": v(-61.04, 48.96) * mm, "construction": true});
            skLineSegment(sketch, "E32", {"start": v(-61.04, 48.96) * mm, "end": v(-48.96, 61.04) * mm, "construction": true});
            skPoint(sketch, "E33", {"position": v(55, 55) * mm});
            skPoint(sketch, "E34", {"position": v(-55, -55) * mm});
            skPoint(sketch, "E35", {"position": v(-55, 55) * mm});
            skPoint(sketch, "E36", {"position": v(55, -55) * mm});
            skPoint(sketch, "E37", {"position": v(107.5, 0) * mm});
            skPoint(sketch, "E38", {"position": v(0, -107.5) * mm});
            skPoint(sketch, "E39", {"position": v(-107.5, 0) * mm});
            skPoint(sketch, "E40", {"position": v(0, 107.5) * mm});
            skSolve(sketch);
        }
        {
            var Q0;
            Q0=makeQuery(id+"F0.imprint","IMPRINT",FACE,{"disambiguationData":[TD([[makeQuery(id+"F0.imprint","IMPRINT",EDGE,{"derivedFrom":sQuery(id+"F0.wireOp",EDGE,"E0.bottom")}),-1.0]])]});
            extrude(context, id + "F1", {"entities" : qUnion([Q0]), "oppositeDirection" : true, "depth" : 12 * mm, "offsetDistance" : 25 * mm});
        }
        {
            var Q0;
            Q0=makeQuery(id+"F0.imprint","IMPRINT",FACE,{"disambiguationData":[TD([[makeQuery(id+"F0.imprint","IMPRINT",EDGE,{"derivedFrom":sQuery(id+"F0.wireOp",EDGE,"E21.3.3.2")}),-1.0]])]});
            var Q1;
            Q1=makeQuery(id+"F0.imprint","IMPRINT",FACE,{"disambiguationData":[TD([[makeQuery(id+"F0.imprint","IMPRINT",EDGE,{"derivedFrom":sQuery(id+"F0.wireOp",EDGE,"E21.2.3.2")}),-1.0]])]});
            var Q2;
            Q2=makeQuery(id+"F0.imprint","IMPRINT",FACE,{"disambiguationData":[TD([[makeQuery(id+"F0.imprint","IMPRINT",EDGE,{"derivedFrom":sQuery(id+"F0.wireOp",EDGE,"E0.bottom")}),-1.0]])]});
            var Q3;
            Q3=makeQuery(id+"F0.imprint","IMPRINT",FACE,{"disambiguationData":[TD([[makeQuery(id+"F0.imprint","IMPRINT",EDGE,{"derivedFrom":sQuery(id+"F0.wireOp",EDGE,"E21.1.3.2")}),-1.0]])]});
            var Q4;
            Q4=makeQuery(id+"F0.imprint","IMPRINT",FACE,{"disambiguationData":[TD([[makeQuery(id+"F0.imprint","IMPRINT",EDGE,{"derivedFrom":sQuery(id+"F0.wireOp",EDGE,"E21.0.3.2")}),-1.0]])]});
            var Q5;
            Q5=makeQuery(id+"F0.imprint","IMPRINT",FACE,{"disambiguationData":[TD([[makeQuery(id+"F0.imprint","IMPRINT",EDGE,{"derivedFrom":sQuery(id+"F0.wireOp",EDGE,"E21.1.2.2")}),-1.0]])]});
            var Q6;
            Q6=makeQuery(id+"F0.imprint","IMPRINT",FACE,{"disambiguationData":[TD([[makeQuery(id+"F0.imprint","IMPRINT",EDGE,{"derivedFrom":sQuery(id+"F0.wireOp",EDGE,"E21.0.2.2")}),-1.0]])]});
            var Q7;
            Q7=makeQuery(id+"F0.imprint","IMPRINT",FACE,{"disambiguationData":[TD([[makeQuery(id+"F0.imprint","IMPRINT",EDGE,{"derivedFrom":sQuery(id+"F0.wireOp",EDGE,"E21.2.2.2")}),-1.0]])]});
            var Q8;
            Q8=makeQuery(id+"F0.imprint","IMPRINT",FACE,{"disambiguationData":[TD([[makeQuery(id+"F0.imprint","IMPRINT",EDGE,{"derivedFrom":sQuery(id+"F0.wireOp",EDGE,"E21.3.2.2")}),-1.0]])]});
            var Q9;
            Q9=makeQuery(id+"F0.imprint","IMPRINT",FACE,{"disambiguationData":[TD([[makeQuery(id+"F0.imprint","IMPRINT",EDGE,{"derivedFrom":sQuery(id+"F0.wireOp",EDGE,"E21.3.1.2")}),-1.0]])]});
            var Q10;
            Q10=makeQuery(id+"F0.imprint","IMPRINT",FACE,{"disambiguationData":[TD([[makeQuery(id+"F0.imprint","IMPRINT",EDGE,{"derivedFrom":sQuery(id+"F0.wireOp",EDGE,"E21.2.1.2")}),-1.0]])]});
            var Q11;
            Q11=makeQuery(id+"F0.imprint","IMPRINT",FACE,{"disambiguationData":[TD([[makeQuery(id+"F0.imprint","IMPRINT",EDGE,{"derivedFrom":sQuery(id+"F0.wireOp",EDGE,"E21.1.1.2")}),-1.0]])]});
            var Q12;
            Q12=makeQuery(id+"F0.imprint","IMPRINT",FACE,{"disambiguationData":[TD([[makeQuery(id+"F0.imprint","IMPRINT",EDGE,{"derivedFrom":sQuery(id+"F0.wireOp",EDGE,"E21.0.1.2")}),-1.0]])]});
            var Q13;
            Q13=makeQuery(id+"F0.imprint","IMPRINT",FACE,{"disambiguationData":[TD([[makeQuery(id+"F0.imprint","IMPRINT",EDGE,{"derivedFrom":sQuery(id+"F0.wireOp",EDGE,"E4")}),-1.0]])]});
            var Q14;
            Q14=makeQuery(id+"F0.imprint","IMPRINT",FACE,{"disambiguationData":[TD([[makeQuery(id+"F0.imprint","IMPRINT",EDGE,{"derivedFrom":sQuery(id+"F0.wireOp",EDGE,"E21.1.0.2")}),-1.0]])]});
            var Q15;
            Q15=makeQuery(id+"F0.imprint","IMPRINT",FACE,{"disambiguationData":[TD([[makeQuery(id+"F0.imprint","IMPRINT",EDGE,{"derivedFrom":sQuery(id+"F0.wireOp",EDGE,"E21.2.0.2")}),-1.0]])]});
            var Q16;
            Q16=makeQuery(id+"F0.imprint","IMPRINT",FACE,{"disambiguationData":[TD([[makeQuery(id+"F0.imprint","IMPRINT",EDGE,{"derivedFrom":sQuery(id+"F0.wireOp",EDGE,"E21.3.0.2")}),-1.0]])]});
            extrude(context, id + "F2", {"entities" : qUnion([Q0, Q1, Q2, Q3, Q4, Q5, Q6, Q7, Q8, Q9, Q10, Q11, Q12, Q13, Q14, Q15, Q16]), "oppositeDirection" : true, "depth" : 18 * mm, "offsetDistance" : 25 * mm, "hasSecondDirection" : true, "secondDirectionOppositeDirection" : true, "secondDirectionDepth" : 12 * mm});
        }
        {
            var Q0;
            Q0=makeQuery(id+"F0.imprint","IMPRINT",FACE,{"disambiguationData":[TD([[makeQuery(id+"F0.imprint","IMPRINT",EDGE,{"derivedFrom":sQuery(id+"F0.wireOp",EDGE,"E4")}),-1.0]])]});
            var Q1;
            Q1=makeQuery(id+"F0.imprint","IMPRINT",FACE,{"disambiguationData":[TD([[makeQuery(id+"F0.imprint","IMPRINT",EDGE,{"derivedFrom":sQuery(id+"F0.wireOp",EDGE,"E21.1.0.2")}),-1.0]])]});
            var Q2;
            Q2=makeQuery(id+"F0.imprint","IMPRINT",FACE,{"disambiguationData":[TD([[makeQuery(id+"F0.imprint","IMPRINT",EDGE,{"derivedFrom":sQuery(id+"F0.wireOp",EDGE,"E21.2.0.2")}),-1.0]])]});
            var Q3;
            Q3=makeQuery(id+"F0.imprint","IMPRINT",FACE,{"disambiguationData":[TD([[makeQuery(id+"F0.imprint","IMPRINT",EDGE,{"derivedFrom":sQuery(id+"F0.wireOp",EDGE,"E21.3.0.2")}),-1.0]])]});
            var Q4;
            Q4=makeQuery(id+"F0.imprint","IMPRINT",FACE,{"disambiguationData":[TD([[makeQuery(id+"F0.imprint","IMPRINT",EDGE,{"derivedFrom":sQuery(id+"F0.wireOp",EDGE,"E21.0.1.2")}),-1.0]])]});
            var Q5;
            Q5=makeQuery(id+"F0.imprint","IMPRINT",FACE,{"disambiguationData":[TD([[makeQuery(id+"F0.imprint","IMPRINT",EDGE,{"derivedFrom":sQuery(id+"F0.wireOp",EDGE,"E21.1.1.2")}),-1.0]])]});
            var Q6;
            Q6=makeQuery(id+"F0.imprint","IMPRINT",FACE,{"disambiguationData":[TD([[makeQuery(id+"F0.imprint","IMPRINT",EDGE,{"derivedFrom":sQuery(id+"F0.wireOp",EDGE,"E21.2.1.2")}),-1.0]])]});
            var Q7;
            Q7=makeQuery(id+"F0.imprint","IMPRINT",FACE,{"disambiguationData":[TD([[makeQuery(id+"F0.imprint","IMPRINT",EDGE,{"derivedFrom":sQuery(id+"F0.wireOp",EDGE,"E21.3.1.2")}),-1.0]])]});
            var Q8;
            Q8=makeQuery(id+"F0.imprint","IMPRINT",FACE,{"disambiguationData":[TD([[makeQuery(id+"F0.imprint","IMPRINT",EDGE,{"derivedFrom":sQuery(id+"F0.wireOp",EDGE,"E21.3.2.2")}),-1.0]])]});
            var Q9;
            Q9=makeQuery(id+"F0.imprint","IMPRINT",FACE,{"disambiguationData":[TD([[makeQuery(id+"F0.imprint","IMPRINT",EDGE,{"derivedFrom":sQuery(id+"F0.wireOp",EDGE,"E21.2.2.2")}),-1.0]])]});
            var Q10;
            Q10=makeQuery(id+"F0.imprint","IMPRINT",FACE,{"disambiguationData":[TD([[makeQuery(id+"F0.imprint","IMPRINT",EDGE,{"derivedFrom":sQuery(id+"F0.wireOp",EDGE,"E21.1.2.2")}),-1.0]])]});
            var Q11;
            Q11=makeQuery(id+"F0.imprint","IMPRINT",FACE,{"disambiguationData":[TD([[makeQuery(id+"F0.imprint","IMPRINT",EDGE,{"derivedFrom":sQuery(id+"F0.wireOp",EDGE,"E21.0.2.2")}),-1.0]])]});
            var Q12;
            Q12=makeQuery(id+"F0.imprint","IMPRINT",FACE,{"disambiguationData":[TD([[makeQuery(id+"F0.imprint","IMPRINT",EDGE,{"derivedFrom":sQuery(id+"F0.wireOp",EDGE,"E21.0.3.2")}),-1.0]])]});
            var Q13;
            Q13=makeQuery(id+"F0.imprint","IMPRINT",FACE,{"disambiguationData":[TD([[makeQuery(id+"F0.imprint","IMPRINT",EDGE,{"derivedFrom":sQuery(id+"F0.wireOp",EDGE,"E21.1.3.2")}),-1.0]])]});
            var Q14;
            Q14=makeQuery(id+"F0.imprint","IMPRINT",FACE,{"disambiguationData":[TD([[makeQuery(id+"F0.imprint","IMPRINT",EDGE,{"derivedFrom":sQuery(id+"F0.wireOp",EDGE,"E21.2.3.2")}),-1.0]])]});
            var Q15;
            Q15=makeQuery(id+"F0.imprint","IMPRINT",FACE,{"disambiguationData":[TD([[makeQuery(id+"F0.imprint","IMPRINT",EDGE,{"derivedFrom":sQuery(id+"F0.wireOp",EDGE,"E21.3.3.2")}),-1.0]])]});
            extrude(context, id + "F3", {"entities" : qUnion([Q0, Q1, Q2, Q3, Q4, Q5, Q6, Q7, Q8, Q9, Q10, Q11, Q12, Q13, Q14, Q15]), "oppositeDirection" : true, "depth" : 6 * mm, "offsetDistance" : 25 * mm});
        }
        {
            var Q0;
            Q0=makeQuery(id+"F0.imprint","IMPRINT",FACE,{"disambiguationData":[TD([[makeQuery(id+"F0.imprint","IMPRINT",EDGE,{"derivedFrom":sQuery(id+"F0.wireOp",EDGE,"E21.1.0.8")}),1.0]])]});
            var Q1;
            Q1=makeQuery(id+"F0.imprint","IMPRINT",FACE,{"disambiguationData":[TD([[makeQuery(id+"F0.imprint","IMPRINT",EDGE,{"derivedFrom":sQuery(id+"F0.wireOp",EDGE,"E21.2.0.8")}),1.0]])]});
            var Q2;
            Q2=makeQuery(id+"F0.imprint","IMPRINT",FACE,{"disambiguationData":[TD([[makeQuery(id+"F0.imprint","IMPRINT",EDGE,{"derivedFrom":sQuery(id+"F0.wireOp",EDGE,"E21.3.0.8")}),1.0]])]});
            var Q3;
            Q3=makeQuery(id+"F0.imprint","IMPRINT",FACE,{"disambiguationData":[TD([[makeQuery(id+"F0.imprint","IMPRINT",EDGE,{"derivedFrom":sQuery(id+"F0.wireOp",EDGE,"E21.0.1.8")}),1.0]])]});
            var Q4;
            Q4=makeQuery(id+"F0.imprint","IMPRINT",FACE,{"disambiguationData":[TD([[makeQuery(id+"F0.imprint","IMPRINT",EDGE,{"derivedFrom":sQuery(id+"F0.wireOp",EDGE,"E21.1.1.8")}),1.0]])]});
            var Q5;
            Q5=makeQuery(id+"F0.imprint","IMPRINT",FACE,{"disambiguationData":[TD([[makeQuery(id+"F0.imprint","IMPRINT",EDGE,{"derivedFrom":sQuery(id+"F0.wireOp",EDGE,"E21.2.1.8")}),1.0]])]});
            var Q6;
            Q6=makeQuery(id+"F0.imprint","IMPRINT",FACE,{"disambiguationData":[TD([[makeQuery(id+"F0.imprint","IMPRINT",EDGE,{"derivedFrom":sQuery(id+"F0.wireOp",EDGE,"E21.3.1.8")}),1.0]])]});
            var Q7;
            Q7=makeQuery(id+"F0.imprint","IMPRINT",FACE,{"disambiguationData":[TD([[makeQuery(id+"F0.imprint","IMPRINT",EDGE,{"derivedFrom":sQuery(id+"F0.wireOp",EDGE,"E21.0.2.8")}),1.0]])]});
            var Q8;
            Q8=makeQuery(id+"F0.imprint","IMPRINT",FACE,{"disambiguationData":[TD([[makeQuery(id+"F0.imprint","IMPRINT",EDGE,{"derivedFrom":sQuery(id+"F0.wireOp",EDGE,"E21.1.2.8")}),1.0]])]});
            var Q9;
            Q9=makeQuery(id+"F0.imprint","IMPRINT",FACE,{"disambiguationData":[TD([[makeQuery(id+"F0.imprint","IMPRINT",EDGE,{"derivedFrom":sQuery(id+"F0.wireOp",EDGE,"E21.2.2.8")}),1.0]])]});
            var Q10;
            Q10=makeQuery(id+"F0.imprint","IMPRINT",FACE,{"disambiguationData":[TD([[makeQuery(id+"F0.imprint","IMPRINT",EDGE,{"derivedFrom":sQuery(id+"F0.wireOp",EDGE,"E21.3.2.8")}),1.0]])]});
            var Q11;
            Q11=makeQuery(id+"F0.imprint","IMPRINT",FACE,{"disambiguationData":[TD([[makeQuery(id+"F0.imprint","IMPRINT",EDGE,{"derivedFrom":sQuery(id+"F0.wireOp",EDGE,"E21.0.3.8")}),1.0]])]});
            var Q12;
            Q12=makeQuery(id+"F0.imprint","IMPRINT",FACE,{"disambiguationData":[TD([[makeQuery(id+"F0.imprint","IMPRINT",EDGE,{"derivedFrom":sQuery(id+"F0.wireOp",EDGE,"E21.1.3.8")}),1.0]])]});
            var Q13;
            Q13=makeQuery(id+"F0.imprint","IMPRINT",FACE,{"disambiguationData":[TD([[makeQuery(id+"F0.imprint","IMPRINT",EDGE,{"derivedFrom":sQuery(id+"F0.wireOp",EDGE,"E21.2.3.8")}),1.0]])]});
            var Q14;
            Q14=makeQuery(id+"F0.imprint","IMPRINT",FACE,{"disambiguationData":[TD([[makeQuery(id+"F0.imprint","IMPRINT",EDGE,{"derivedFrom":sQuery(id+"F0.wireOp",EDGE,"E21.3.3.8")}),1.0]])]});
            var Q15;
            Q15=makeQuery(id+"F0.imprint","IMPRINT",FACE,{"disambiguationData":[TD([[makeQuery(id+"F0.imprint","IMPRINT",EDGE,{"derivedFrom":sQuery(id+"F0.wireOp",EDGE,"E20")}),1.0]])]});
            extrude(context, id + "F4", {"entities" : qUnion([Q0, Q1, Q2, Q3, Q4, Q5, Q6, Q7, Q8, Q9, Q10, Q11, Q12, Q13, Q14, Q15]), "oppositeDirection" : true, "depth" : 20 * mm, "offsetDistance" : 25 * mm, "hasSecondDirection" : true, "secondDirectionOppositeDirection" : false, "secondDirectionDepth" : 5 * mm});
        }
        {
            var Q0;
            Q0=makeQuery(id+"F0.imprint","IMPRINT",FACE,{"disambiguationData":[TD([[makeQuery(id+"F0.imprint","IMPRINT",EDGE,{"derivedFrom":sQuery(id+"F0.wireOp",EDGE,"E0.bottom")}),-1.0]])]});
            var sketch = newSketch(context, id + "F5", { "sketchPlane" : qUnion([Q0])});
            skLineSegment(sketch, "E41.bottom", {"start": v(-122.5, 132.5) * mm, "end": v(122.5, 132.5) * mm});
            skLineSegment(sketch, "E41.top", {"start": v(-122.5, -132.5) * mm, "end": v(122.5, -132.5) * mm});
            skLineSegment(sketch, "E41.left", {"start": v(-132.5, 122.5) * mm, "end": v(-132.5, -122.5) * mm});
            skLineSegment(sketch, "E41.right", {"start": v(132.5, 122.5) * mm, "end": v(132.5, -122.5) * mm});
            skPoint(sketch, "E42.visualSharp", {"position": v(-132.5, 132.5) * mm});
            skArc(sketch, "E42.filletArc", {"start": v(-122.5, 132.5) * mm, "mid": v(-129.57, 129.57) * mm, "end": v(-132.5, 122.5) * mm});
            skPoint(sketch, "E43.visualSharp", {"position": v(132.5, 132.5) * mm});
            skArc(sketch, "E43.filletArc", {"start": v(132.5, 122.5) * mm, "mid": v(129.57, 129.57) * mm, "end": v(122.5, 132.5) * mm});
            skPoint(sketch, "E44.visualSharp", {"position": v(132.5, -132.5) * mm});
            skArc(sketch, "E44.filletArc", {"start": v(122.5, -132.5) * mm, "mid": v(129.57, -129.57) * mm, "end": v(132.5, -122.5) * mm});
            skPoint(sketch, "E45.visualSharp", {"position": v(-132.5, -132.5) * mm});
            skArc(sketch, "E45.filletArc", {"start": v(-132.5, -122.5) * mm, "mid": v(-129.57, -129.57) * mm, "end": v(-122.5, -132.5) * mm});
            skCircle(sketch, "E46", {"center": v(-122.5, 122.5) * mm, "radius": 2.5 * mm});
            skCircle(sketch, "E47.0.1.0", {"center": v(-122.5, -122.5) * mm, "radius": 2.5 * mm});
            skCircle(sketch, "E47.1.0.0", {"center": v(122.5, 122.5) * mm, "radius": 2.5 * mm});
            skCircle(sketch, "E47.1.1.0", {"center": v(122.5, -122.5) * mm, "radius": 2.5 * mm});
            skLineSegment(sketch, "E47.direction1", {"start": v(-122.5, 122.5) * mm, "end": v(122.5, 122.5) * mm, "construction": true});
            skLineSegment(sketch, "E47.direction2", {"start": v(-122.5, 122.5) * mm, "end": v(-122.5, -122.5) * mm, "construction": true});
            skLineSegment(sketch, "E48", {"start": v(-100.01, 106.5) * mm, "end": v(-64.99, 106.5) * mm});
            skLineSegment(sketch, "E49", {"start": v(-64.99, 106.5) * mm, "end": v(-58.5, 100.01) * mm});
            skLineSegment(sketch, "E50", {"start": v(-58.5, 100.01) * mm, "end": v(-58.5, 64.99) * mm});
            skLineSegment(sketch, "E51", {"start": v(-58.5, 64.99) * mm, "end": v(-64.99, 58.5) * mm});
            skLineSegment(sketch, "E52", {"start": v(-64.99, 58.5) * mm, "end": v(-100.01, 58.5) * mm});
            skLineSegment(sketch, "E53", {"start": v(-100.01, 58.5) * mm, "end": v(-106.5, 64.99) * mm});
            skLineSegment(sketch, "E54", {"start": v(-106.5, 64.99) * mm, "end": v(-106.5, 100.01) * mm});
            skLineSegment(sketch, "E55", {"start": v(-106.5, 100.01) * mm, "end": v(-100.01, 106.5) * mm});
            skLineSegment(sketch, "E56.0.1.0", {"start": v(-64.99, 3.5) * mm, "end": v(-100.01, 3.5) * mm});
            skLineSegment(sketch, "E56.0.1.1", {"start": v(-106.5, 45.01) * mm, "end": v(-100.01, 51.5) * mm});
            skLineSegment(sketch, "E56.0.1.2", {"start": v(-58.5, 45.01) * mm, "end": v(-58.5, 9.99) * mm});
            skLineSegment(sketch, "E56.0.1.3", {"start": v(-58.5, 9.99) * mm, "end": v(-64.99, 3.5) * mm});
            skLineSegment(sketch, "E56.0.1.4", {"start": v(-100.01, 51.5) * mm, "end": v(-64.99, 51.5) * mm});
            skLineSegment(sketch, "E56.0.1.5", {"start": v(-106.5, 9.99) * mm, "end": v(-106.5, 45.01) * mm});
            skLineSegment(sketch, "E56.0.1.6", {"start": v(-100.01, 3.5) * mm, "end": v(-106.5, 9.99) * mm});
            skLineSegment(sketch, "E56.0.1.7", {"start": v(-64.99, 51.5) * mm, "end": v(-58.5, 45.01) * mm});
            skLineSegment(sketch, "E56.0.2.0", {"start": v(-64.99, -51.5) * mm, "end": v(-100.01, -51.5) * mm});
            skLineSegment(sketch, "E56.0.2.1", {"start": v(-106.5, -9.99) * mm, "end": v(-100.01, -3.5) * mm});
            skLineSegment(sketch, "E56.0.2.2", {"start": v(-58.5, -9.99) * mm, "end": v(-58.5, -45.01) * mm});
            skLineSegment(sketch, "E56.0.2.3", {"start": v(-58.5, -45.01) * mm, "end": v(-64.99, -51.5) * mm});
            skLineSegment(sketch, "E56.0.2.4", {"start": v(-100.01, -3.5) * mm, "end": v(-64.99, -3.5) * mm});
            skLineSegment(sketch, "E56.0.2.5", {"start": v(-106.5, -45.01) * mm, "end": v(-106.5, -9.99) * mm});
            skLineSegment(sketch, "E56.0.2.6", {"start": v(-100.01, -51.5) * mm, "end": v(-106.5, -45.01) * mm});
            skLineSegment(sketch, "E56.0.2.7", {"start": v(-64.99, -3.5) * mm, "end": v(-58.5, -9.99) * mm});
            skLineSegment(sketch, "E56.0.3.0", {"start": v(-64.99, -106.5) * mm, "end": v(-100.01, -106.5) * mm});
            skLineSegment(sketch, "E56.0.3.1", {"start": v(-106.5, -64.99) * mm, "end": v(-100.01, -58.5) * mm});
            skLineSegment(sketch, "E56.0.3.2", {"start": v(-58.5, -64.99) * mm, "end": v(-58.5, -100.01) * mm});
            skLineSegment(sketch, "E56.0.3.3", {"start": v(-58.5, -100.01) * mm, "end": v(-64.99, -106.5) * mm});
            skLineSegment(sketch, "E56.0.3.4", {"start": v(-100.01, -58.5) * mm, "end": v(-64.99, -58.5) * mm});
            skLineSegment(sketch, "E56.0.3.5", {"start": v(-106.5, -100.01) * mm, "end": v(-106.5, -64.99) * mm});
            skLineSegment(sketch, "E56.0.3.6", {"start": v(-100.01, -106.5) * mm, "end": v(-106.5, -100.01) * mm});
            skLineSegment(sketch, "E56.0.3.7", {"start": v(-64.99, -58.5) * mm, "end": v(-58.5, -64.99) * mm});
            skLineSegment(sketch, "E56.1.0.0", {"start": v(-9.99, 58.5) * mm, "end": v(-45.01, 58.5) * mm});
            skLineSegment(sketch, "E56.1.0.1", {"start": v(-51.5, 100.01) * mm, "end": v(-45.01, 106.5) * mm});
            skLineSegment(sketch, "E56.1.0.2", {"start": v(-3.5, 100.01) * mm, "end": v(-3.5, 64.99) * mm});
            skLineSegment(sketch, "E56.1.0.3", {"start": v(-3.5, 64.99) * mm, "end": v(-9.99, 58.5) * mm});
            skLineSegment(sketch, "E56.1.0.4", {"start": v(-45.01, 106.5) * mm, "end": v(-9.99, 106.5) * mm});
            skLineSegment(sketch, "E56.1.0.5", {"start": v(-51.5, 64.99) * mm, "end": v(-51.5, 100.01) * mm});
            skLineSegment(sketch, "E56.1.0.6", {"start": v(-45.01, 58.5) * mm, "end": v(-51.5, 64.99) * mm});
            skLineSegment(sketch, "E56.1.0.7", {"start": v(-9.99, 106.5) * mm, "end": v(-3.5, 100.01) * mm});
            skLineSegment(sketch, "E56.1.1.0", {"start": v(-9.99, 3.5) * mm, "end": v(-45.01, 3.5) * mm});
            skLineSegment(sketch, "E56.1.1.1", {"start": v(-51.5, 45.01) * mm, "end": v(-45.01, 51.5) * mm});
            skLineSegment(sketch, "E56.1.1.2", {"start": v(-3.5, 45.01) * mm, "end": v(-3.5, 9.99) * mm});
            skLineSegment(sketch, "E56.1.1.3", {"start": v(-3.5, 9.99) * mm, "end": v(-9.99, 3.5) * mm});
            skLineSegment(sketch, "E56.1.1.4", {"start": v(-45.01, 51.5) * mm, "end": v(-9.99, 51.5) * mm});
            skLineSegment(sketch, "E56.1.1.5", {"start": v(-51.5, 9.99) * mm, "end": v(-51.5, 45.01) * mm});
            skLineSegment(sketch, "E56.1.1.6", {"start": v(-45.01, 3.5) * mm, "end": v(-51.5, 9.99) * mm});
            skLineSegment(sketch, "E56.1.1.7", {"start": v(-9.99, 51.5) * mm, "end": v(-3.5, 45.01) * mm});
            skLineSegment(sketch, "E56.1.2.0", {"start": v(-9.99, -51.5) * mm, "end": v(-45.01, -51.5) * mm});
            skLineSegment(sketch, "E56.1.2.1", {"start": v(-51.5, -9.99) * mm, "end": v(-45.01, -3.5) * mm});
            skLineSegment(sketch, "E56.1.2.2", {"start": v(-3.5, -9.99) * mm, "end": v(-3.5, -45.01) * mm});
            skLineSegment(sketch, "E56.1.2.3", {"start": v(-3.5, -45.01) * mm, "end": v(-9.99, -51.5) * mm});
            skLineSegment(sketch, "E56.1.2.4", {"start": v(-45.01, -3.5) * mm, "end": v(-9.99, -3.5) * mm});
            skLineSegment(sketch, "E56.1.2.5", {"start": v(-51.5, -45.01) * mm, "end": v(-51.5, -9.99) * mm});
            skLineSegment(sketch, "E56.1.2.6", {"start": v(-45.01, -51.5) * mm, "end": v(-51.5, -45.01) * mm});
            skLineSegment(sketch, "E56.1.2.7", {"start": v(-9.99, -3.5) * mm, "end": v(-3.5, -9.99) * mm});
            skLineSegment(sketch, "E56.1.3.0", {"start": v(-9.99, -106.5) * mm, "end": v(-45.01, -106.5) * mm});
            skLineSegment(sketch, "E56.1.3.1", {"start": v(-51.5, -64.99) * mm, "end": v(-45.01, -58.5) * mm});
            skLineSegment(sketch, "E56.1.3.2", {"start": v(-3.5, -64.99) * mm, "end": v(-3.5, -100.01) * mm});
            skLineSegment(sketch, "E56.1.3.3", {"start": v(-3.5, -100.01) * mm, "end": v(-9.99, -106.5) * mm});
            skLineSegment(sketch, "E56.1.3.4", {"start": v(-45.01, -58.5) * mm, "end": v(-9.99, -58.5) * mm});
            skLineSegment(sketch, "E56.1.3.5", {"start": v(-51.5, -100.01) * mm, "end": v(-51.5, -64.99) * mm});
            skLineSegment(sketch, "E56.1.3.6", {"start": v(-45.01, -106.5) * mm, "end": v(-51.5, -100.01) * mm});
            skLineSegment(sketch, "E56.1.3.7", {"start": v(-9.99, -58.5) * mm, "end": v(-3.5, -64.99) * mm});
            skLineSegment(sketch, "E56.2.0.0", {"start": v(45.01, 58.5) * mm, "end": v(9.99, 58.5) * mm});
            skLineSegment(sketch, "E56.2.0.1", {"start": v(3.5, 100.01) * mm, "end": v(9.99, 106.5) * mm});
            skLineSegment(sketch, "E56.2.0.2", {"start": v(51.5, 100.01) * mm, "end": v(51.5, 64.99) * mm});
            skLineSegment(sketch, "E56.2.0.3", {"start": v(51.5, 64.99) * mm, "end": v(45.01, 58.5) * mm});
            skLineSegment(sketch, "E56.2.0.4", {"start": v(9.99, 106.5) * mm, "end": v(45.01, 106.5) * mm});
            skLineSegment(sketch, "E56.2.0.5", {"start": v(3.5, 64.99) * mm, "end": v(3.5, 100.01) * mm});
            skLineSegment(sketch, "E56.2.0.6", {"start": v(9.99, 58.5) * mm, "end": v(3.5, 64.99) * mm});
            skLineSegment(sketch, "E56.2.0.7", {"start": v(45.01, 106.5) * mm, "end": v(51.5, 100.01) * mm});
            skLineSegment(sketch, "E56.2.1.0", {"start": v(45.01, 3.5) * mm, "end": v(9.99, 3.5) * mm});
            skLineSegment(sketch, "E56.2.1.1", {"start": v(3.5, 45.01) * mm, "end": v(9.99, 51.5) * mm});
            skLineSegment(sketch, "E56.2.1.2", {"start": v(51.5, 45.01) * mm, "end": v(51.5, 9.99) * mm});
            skLineSegment(sketch, "E56.2.1.3", {"start": v(51.5, 9.99) * mm, "end": v(45.01, 3.5) * mm});
            skLineSegment(sketch, "E56.2.1.4", {"start": v(9.99, 51.5) * mm, "end": v(45.01, 51.5) * mm});
            skLineSegment(sketch, "E56.2.1.5", {"start": v(3.5, 9.99) * mm, "end": v(3.5, 45.01) * mm});
            skLineSegment(sketch, "E56.2.1.6", {"start": v(9.99, 3.5) * mm, "end": v(3.5, 9.99) * mm});
            skLineSegment(sketch, "E56.2.1.7", {"start": v(45.01, 51.5) * mm, "end": v(51.5, 45.01) * mm});
            skLineSegment(sketch, "E56.2.2.0", {"start": v(45.01, -51.5) * mm, "end": v(9.99, -51.5) * mm});
            skLineSegment(sketch, "E56.2.2.1", {"start": v(3.5, -9.99) * mm, "end": v(9.99, -3.5) * mm});
            skLineSegment(sketch, "E56.2.2.2", {"start": v(51.5, -9.99) * mm, "end": v(51.5, -45.01) * mm});
            skLineSegment(sketch, "E56.2.2.3", {"start": v(51.5, -45.01) * mm, "end": v(45.01, -51.5) * mm});
            skLineSegment(sketch, "E56.2.2.4", {"start": v(9.99, -3.5) * mm, "end": v(45.01, -3.5) * mm});
            skLineSegment(sketch, "E56.2.2.5", {"start": v(3.5, -45.01) * mm, "end": v(3.5, -9.99) * mm});
            skLineSegment(sketch, "E56.2.2.6", {"start": v(9.99, -51.5) * mm, "end": v(3.5, -45.01) * mm});
            skLineSegment(sketch, "E56.2.2.7", {"start": v(45.01, -3.5) * mm, "end": v(51.5, -9.99) * mm});
            skLineSegment(sketch, "E56.2.3.0", {"start": v(45.01, -106.5) * mm, "end": v(9.99, -106.5) * mm});
            skLineSegment(sketch, "E56.2.3.1", {"start": v(3.5, -64.99) * mm, "end": v(9.99, -58.5) * mm});
            skLineSegment(sketch, "E56.2.3.2", {"start": v(51.5, -64.99) * mm, "end": v(51.5, -100.01) * mm});
            skLineSegment(sketch, "E56.2.3.3", {"start": v(51.5, -100.01) * mm, "end": v(45.01, -106.5) * mm});
            skLineSegment(sketch, "E56.2.3.4", {"start": v(9.99, -58.5) * mm, "end": v(45.01, -58.5) * mm});
            skLineSegment(sketch, "E56.2.3.5", {"start": v(3.5, -100.01) * mm, "end": v(3.5, -64.99) * mm});
            skLineSegment(sketch, "E56.2.3.6", {"start": v(9.99, -106.5) * mm, "end": v(3.5, -100.01) * mm});
            skLineSegment(sketch, "E56.2.3.7", {"start": v(45.01, -58.5) * mm, "end": v(51.5, -64.99) * mm});
            skLineSegment(sketch, "E56.3.0.0", {"start": v(100.01, 58.5) * mm, "end": v(64.99, 58.5) * mm});
            skLineSegment(sketch, "E56.3.0.1", {"start": v(58.5, 100.01) * mm, "end": v(64.99, 106.5) * mm});
            skLineSegment(sketch, "E56.3.0.2", {"start": v(106.5, 100.01) * mm, "end": v(106.5, 64.99) * mm});
            skLineSegment(sketch, "E56.3.0.3", {"start": v(106.5, 64.99) * mm, "end": v(100.01, 58.5) * mm});
            skLineSegment(sketch, "E56.3.0.4", {"start": v(64.99, 106.5) * mm, "end": v(100.01, 106.5) * mm});
            skLineSegment(sketch, "E56.3.0.5", {"start": v(58.5, 64.99) * mm, "end": v(58.5, 100.01) * mm});
            skLineSegment(sketch, "E56.3.0.6", {"start": v(64.99, 58.5) * mm, "end": v(58.5, 64.99) * mm});
            skLineSegment(sketch, "E56.3.0.7", {"start": v(100.01, 106.5) * mm, "end": v(106.5, 100.01) * mm});
            skLineSegment(sketch, "E56.3.1.0", {"start": v(100.01, 3.5) * mm, "end": v(64.99, 3.5) * mm});
            skLineSegment(sketch, "E56.3.1.1", {"start": v(58.5, 45.01) * mm, "end": v(64.99, 51.5) * mm});
            skLineSegment(sketch, "E56.3.1.2", {"start": v(106.5, 45.01) * mm, "end": v(106.5, 9.99) * mm});
            skLineSegment(sketch, "E56.3.1.3", {"start": v(106.5, 9.99) * mm, "end": v(100.01, 3.5) * mm});
            skLineSegment(sketch, "E56.3.1.4", {"start": v(64.99, 51.5) * mm, "end": v(100.01, 51.5) * mm});
            skLineSegment(sketch, "E56.3.1.5", {"start": v(58.5, 9.99) * mm, "end": v(58.5, 45.01) * mm});
            skLineSegment(sketch, "E56.3.1.6", {"start": v(64.99, 3.5) * mm, "end": v(58.5, 9.99) * mm});
            skLineSegment(sketch, "E56.3.1.7", {"start": v(100.01, 51.5) * mm, "end": v(106.5, 45.01) * mm});
            skLineSegment(sketch, "E56.3.2.0", {"start": v(100.01, -51.5) * mm, "end": v(64.99, -51.5) * mm});
            skLineSegment(sketch, "E56.3.2.1", {"start": v(58.5, -9.99) * mm, "end": v(64.99, -3.5) * mm});
            skLineSegment(sketch, "E56.3.2.2", {"start": v(106.5, -9.99) * mm, "end": v(106.5, -45.01) * mm});
            skLineSegment(sketch, "E56.3.2.3", {"start": v(106.5, -45.01) * mm, "end": v(100.01, -51.5) * mm});
            skLineSegment(sketch, "E56.3.2.4", {"start": v(64.99, -3.5) * mm, "end": v(100.01, -3.5) * mm});
            skLineSegment(sketch, "E56.3.2.5", {"start": v(58.5, -45.01) * mm, "end": v(58.5, -9.99) * mm});
            skLineSegment(sketch, "E56.3.2.6", {"start": v(64.99, -51.5) * mm, "end": v(58.5, -45.01) * mm});
            skLineSegment(sketch, "E56.3.2.7", {"start": v(100.01, -3.5) * mm, "end": v(106.5, -9.99) * mm});
            skLineSegment(sketch, "E56.3.3.0", {"start": v(100.01, -106.5) * mm, "end": v(64.99, -106.5) * mm});
            skLineSegment(sketch, "E56.3.3.1", {"start": v(58.5, -64.99) * mm, "end": v(64.99, -58.5) * mm});
            skLineSegment(sketch, "E56.3.3.2", {"start": v(106.5, -64.99) * mm, "end": v(106.5, -100.01) * mm});
            skLineSegment(sketch, "E56.3.3.3", {"start": v(106.5, -100.01) * mm, "end": v(100.01, -106.5) * mm});
            skLineSegment(sketch, "E56.3.3.4", {"start": v(64.99, -58.5) * mm, "end": v(100.01, -58.5) * mm});
            skLineSegment(sketch, "E56.3.3.5", {"start": v(58.5, -100.01) * mm, "end": v(58.5, -64.99) * mm});
            skLineSegment(sketch, "E56.3.3.6", {"start": v(64.99, -106.5) * mm, "end": v(58.5, -100.01) * mm});
            skLineSegment(sketch, "E56.3.3.7", {"start": v(100.01, -58.5) * mm, "end": v(106.5, -64.99) * mm});
            skLineSegment(sketch, "E56.direction1", {"start": v(-100.01, 58.5) * mm, "end": v(-45.01, 58.5) * mm, "construction": true});
            skLineSegment(sketch, "E56.direction2", {"start": v(-100.01, 58.5) * mm, "end": v(-100.01, 3.5) * mm, "construction": true});
            skSolve(sketch);
        }
        {
            var Q0;
            Q0 = qSketchRegion(id + "F5", true);
            extrude(context, id + "F6", {"entities" : qUnion([Q0]), "depth" : 3 * mm, "offsetDistance" : 25 * mm});
        }
        {
            var Q0;
            Q0=makeQuery(id+"F2.opExtrude","CAP_EDGE",EDGE,{"disambiguationData":[OSD([sQuery(id+"F0.wireOp",EDGE,"E20")])],"isStart":true});
            var Q1;
            Q1=makeQuery(id+"F2.opExtrude","CAP_EDGE",EDGE,{"disambiguationData":[OSD([sQuery(id+"F0.wireOp",EDGE,"E21.1.0.8")])],"isStart":true});
            var Q2;
            Q2=makeQuery(id+"F2.opExtrude","CAP_EDGE",EDGE,{"disambiguationData":[OSD([sQuery(id+"F0.wireOp",EDGE,"E21.2.0.8")])],"isStart":true});
            var Q3;
            Q3=makeQuery(id+"F2.opExtrude","CAP_EDGE",EDGE,{"disambiguationData":[OSD([sQuery(id+"F0.wireOp",EDGE,"E21.3.0.8")])],"isStart":true});
            var Q4;
            Q4=makeQuery(id+"F2.opExtrude","CAP_EDGE",EDGE,{"disambiguationData":[OSD([sQuery(id+"F0.wireOp",EDGE,"E21.3.1.8")])],"isStart":true});
            var Q5;
            Q5=makeQuery(id+"F2.opExtrude","CAP_EDGE",EDGE,{"disambiguationData":[OSD([sQuery(id+"F0.wireOp",EDGE,"E21.2.1.8")])],"isStart":true});
            var Q6;
            Q6=makeQuery(id+"F2.opExtrude","CAP_EDGE",EDGE,{"disambiguationData":[OSD([sQuery(id+"F0.wireOp",EDGE,"E21.1.1.8")])],"isStart":true});
            var Q7;
            Q7=makeQuery(id+"F2.opExtrude","CAP_EDGE",EDGE,{"disambiguationData":[OSD([sQuery(id+"F0.wireOp",EDGE,"E21.0.1.8")])],"isStart":true});
            var Q8;
            Q8=makeQuery(id+"F2.opExtrude","CAP_EDGE",EDGE,{"disambiguationData":[OSD([sQuery(id+"F0.wireOp",EDGE,"E21.0.2.8")])],"isStart":true});
            var Q9;
            Q9=makeQuery(id+"F2.opExtrude","CAP_EDGE",EDGE,{"disambiguationData":[OSD([sQuery(id+"F0.wireOp",EDGE,"E21.1.2.8")])],"isStart":true});
            var Q10;
            Q10=makeQuery(id+"F2.opExtrude","CAP_EDGE",EDGE,{"disambiguationData":[OSD([sQuery(id+"F0.wireOp",EDGE,"E21.2.2.8")])],"isStart":true});
            var Q11;
            Q11=makeQuery(id+"F2.opExtrude","CAP_EDGE",EDGE,{"disambiguationData":[OSD([sQuery(id+"F0.wireOp",EDGE,"E21.3.2.8")])],"isStart":true});
            var Q12;
            Q12=makeQuery(id+"F2.opExtrude","CAP_EDGE",EDGE,{"disambiguationData":[OSD([sQuery(id+"F0.wireOp",EDGE,"E21.3.3.8")])],"isStart":true});
            var Q13;
            Q13=makeQuery(id+"F2.opExtrude","CAP_EDGE",EDGE,{"disambiguationData":[OSD([sQuery(id+"F0.wireOp",EDGE,"E21.2.3.8")])],"isStart":true});
            var Q14;
            Q14=makeQuery(id+"F2.opExtrude","CAP_EDGE",EDGE,{"disambiguationData":[OSD([sQuery(id+"F0.wireOp",EDGE,"E21.1.3.8")])],"isStart":true});
            var Q15;
            Q15=makeQuery(id+"F2.opExtrude","CAP_EDGE",EDGE,{"disambiguationData":[OSD([sQuery(id+"F0.wireOp",EDGE,"E21.0.3.8")])],"isStart":true});
            chamfer(context, id + "F7", {"entities" : qUnion([Q0, Q1, Q2, Q3, Q4, Q5, Q6, Q7, Q8, Q9, Q10, Q11, Q12, Q13, Q14, Q15]), "width" : 2 * mm, "tangentPropagation" : true});
        }
        {
            var Q0;
            Q0=sQuery(id+"F0.wireOp",VERTEX,"E17.filletArc.center");
            var Q1;
            Q1=sQuery(id+"F0.wireOp",VERTEX,"E40");
            var Q2;
            Q2=sQuery(id+"F0.wireOp",VERTEX,"E16.filletArc.center");
            var Q3;
            Q3=sQuery(id+"F0.wireOp",VERTEX,"E39");
            var Q4;
            Q4=sQuery(id+"F0.wireOp",VERTEX,"E37");
            var Q5;
            Q5=sQuery(id+"F0.wireOp",VERTEX,"E18.filletArc.center");
            var Q6;
            Q6=sQuery(id+"F0.wireOp",VERTEX,"E38");
            var Q7;
            Q7=sQuery(id+"F0.wireOp",VERTEX,"E19.filletArc.center");
            var Q8;
            Q8=sQuery(id+"F0.wireOp",VERTEX,"E35");
            var Q9;
            Q9=sQuery(id+"F0.wireOp",VERTEX,"E33");
            var Q10;
            Q10=sQuery(id+"F0.wireOp",VERTEX,"E36");
            var Q11;
            Q11=sQuery(id+"F0.wireOp",VERTEX,"E34");
            var Q12;
            Q12=makeQuery(id+"F1.opExtrude","SWEPT_BODY",BODY,{"disambiguationData":[OSD([sQuery(id+"F0.wireOp",EDGE,"E0.bottom"),sQuery(id+"F0.wireOp",EDGE,"E0.top"),sQuery(id+"F0.wireOp",EDGE,"E0.left"),sQuery(id+"F0.wireOp",EDGE,"E0.right"),sQuery(id+"F0.wireOp",EDGE,"E4"),sQuery(id+"F0.wireOp",EDGE,"E5"),sQuery(id+"F0.wireOp",EDGE,"E6"),sQuery(id+"F0.wireOp",EDGE,"E9.MirrorCS"),sQuery(id+"F0.wireOp",EDGE,"E8.MirrorCS"),sQuery(id+"F0.wireOp",EDGE,"E7.MirrorCS"),sQuery(id+"F0.wireOp",EDGE,"E10.MirrorCS"),sQuery(id+"F0.wireOp",EDGE,"E11.MirrorCS"),sQuery(id+"F0.wireOp",EDGE,"E12.MirrorCS"),sQuery(id+"F0.wireOp",EDGE,"E13.MirrorCS"),sQuery(id+"F0.wireOp",EDGE,"E14.MirrorCS"),sQuery(id+"F0.wireOp",EDGE,"E15.MirrorCS"),sQuery(id+"F0.wireOp",EDGE,"E16.filletArc"),sQuery(id+"F0.wireOp",EDGE,"E17.filletArc"),sQuery(id+"F0.wireOp",EDGE,"E18.filletArc"),sQuery(id+"F0.wireOp",EDGE,"E19.filletArc"),sQuery(id+"F0.wireOp",EDGE,"E21.0.1.2"),sQuery(id+"F0.wireOp",EDGE,"E21.0.1.3"),sQuery(id+"F0.wireOp",EDGE,"E21.0.1.4"),sQuery(id+"F0.wireOp",EDGE,"E21.0.1.5"),sQuery(id+"F0.wireOp",EDGE,"E21.0.1.6"),sQuery(id+"F0.wireOp",EDGE,"E21.0.1.7"),sQuery(id+"F0.wireOp",EDGE,"E21.0.1.9"),sQuery(id+"F0.wireOp",EDGE,"E21.0.1.10"),sQuery(id+"F0.wireOp",EDGE,"E21.0.1.13"),sQuery(id+"F0.wireOp",EDGE,"E21.0.1.14"),sQuery(id+"F0.wireOp",EDGE,"E21.0.1.17"),sQuery(id+"F0.wireOp",EDGE,"E21.0.1.18"),sQuery(id+"F0.wireOp",EDGE,"E21.0.2.2"),sQuery(id+"F0.wireOp",EDGE,"E21.0.2.3"),sQuery(id+"F0.wireOp",EDGE,"E21.0.2.4"),sQuery(id+"F0.wireOp",EDGE,"E21.0.2.5"),sQuery(id+"F0.wireOp",EDGE,"E21.0.2.6"),sQuery(id+"F0.wireOp",EDGE,"E21.0.2.7"),sQuery(id+"F0.wireOp",EDGE,"E21.0.2.9"),sQuery(id+"F0.wireOp",EDGE,"E21.0.2.10"),sQuery(id+"F0.wireOp",EDGE,"E21.0.2.13"),sQuery(id+"F0.wireOp",EDGE,"E21.0.2.14"),sQuery(id+"F0.wireOp",EDGE,"E21.0.2.17"),sQuery(id+"F0.wireOp",EDGE,"E21.0.2.18"),sQuery(id+"F0.wireOp",EDGE,"E21.0.3.2"),sQuery(id+"F0.wireOp",EDGE,"E21.0.3.3"),sQuery(id+"F0.wireOp",EDGE,"E21.0.3.4"),sQuery(id+"F0.wireOp",EDGE,"E21.0.3.5"),sQuery(id+"F0.wireOp",EDGE,"E21.0.3.6"),sQuery(id+"F0.wireOp",EDGE,"E21.0.3.7"),sQuery(id+"F0.wireOp",EDGE,"E21.0.3.9"),sQuery(id+"F0.wireOp",EDGE,"E21.0.3.10"),sQuery(id+"F0.wireOp",EDGE,"E21.0.3.13"),sQuery(id+"F0.wireOp",EDGE,"E21.0.3.14"),sQuery(id+"F0.wireOp",EDGE,"E21.0.3.17"),sQuery(id+"F0.wireOp",EDGE,"E21.0.3.18"),sQuery(id+"F0.wireOp",EDGE,"E21.1.0.2"),sQuery(id+"F0.wireOp",EDGE,"E21.1.0.3"),sQuery(id+"F0.wireOp",EDGE,"E21.1.0.4"),sQuery(id+"F0.wireOp",EDGE,"E21.1.0.5"),sQuery(id+"F0.wireOp",EDGE,"E21.1.0.6"),sQuery(id+"F0.wireOp",EDGE,"E21.1.0.7"),sQuery(id+"F0.wireOp",EDGE,"E21.1.0.9"),sQuery(id+"F0.wireOp",EDGE,"E21.1.0.10"),sQuery(id+"F0.wireOp",EDGE,"E21.1.0.13"),sQuery(id+"F0.wireOp",EDGE,"E21.1.0.14"),sQuery(id+"F0.wireOp",EDGE,"E21.1.0.17"),sQuery(id+"F0.wireOp",EDGE,"E21.1.0.18"),sQuery(id+"F0.wireOp",EDGE,"E21.1.1.2"),sQuery(id+"F0.wireOp",EDGE,"E21.1.1.3"),sQuery(id+"F0.wireOp",EDGE,"E21.1.1.4"),sQuery(id+"F0.wireOp",EDGE,"E21.1.1.5"),sQuery(id+"F0.wireOp",EDGE,"E21.1.1.6"),sQuery(id+"F0.wireOp",EDGE,"E21.1.1.7"),sQuery(id+"F0.wireOp",EDGE,"E21.1.1.9"),sQuery(id+"F0.wireOp",EDGE,"E21.1.1.10"),sQuery(id+"F0.wireOp",EDGE,"E21.1.1.13"),sQuery(id+"F0.wireOp",EDGE,"E21.1.1.14"),sQuery(id+"F0.wireOp",EDGE,"E21.1.1.17"),sQuery(id+"F0.wireOp",EDGE,"E21.1.1.18"),sQuery(id+"F0.wireOp",EDGE,"E21.1.2.2"),sQuery(id+"F0.wireOp",EDGE,"E21.1.2.3"),sQuery(id+"F0.wireOp",EDGE,"E21.1.2.4"),sQuery(id+"F0.wireOp",EDGE,"E21.1.2.5"),sQuery(id+"F0.wireOp",EDGE,"E21.1.2.6"),sQuery(id+"F0.wireOp",EDGE,"E21.1.2.7"),sQuery(id+"F0.wireOp",EDGE,"E21.1.2.9"),sQuery(id+"F0.wireOp",EDGE,"E21.1.2.10"),sQuery(id+"F0.wireOp",EDGE,"E21.1.2.13"),sQuery(id+"F0.wireOp",EDGE,"E21.1.2.14"),sQuery(id+"F0.wireOp",EDGE,"E21.1.2.17"),sQuery(id+"F0.wireOp",EDGE,"E21.1.2.18"),sQuery(id+"F0.wireOp",EDGE,"E21.1.3.2"),sQuery(id+"F0.wireOp",EDGE,"E21.1.3.3"),sQuery(id+"F0.wireOp",EDGE,"E21.1.3.4"),sQuery(id+"F0.wireOp",EDGE,"E21.1.3.5"),sQuery(id+"F0.wireOp",EDGE,"E21.1.3.6"),sQuery(id+"F0.wireOp",EDGE,"E21.1.3.7"),sQuery(id+"F0.wireOp",EDGE,"E21.1.3.9"),sQuery(id+"F0.wireOp",EDGE,"E21.1.3.10"),sQuery(id+"F0.wireOp",EDGE,"E21.1.3.13"),sQuery(id+"F0.wireOp",EDGE,"E21.1.3.14"),sQuery(id+"F0.wireOp",EDGE,"E21.1.3.17"),sQuery(id+"F0.wireOp",EDGE,"E21.1.3.18"),sQuery(id+"F0.wireOp",EDGE,"E21.2.0.2"),sQuery(id+"F0.wireOp",EDGE,"E21.2.0.3"),sQuery(id+"F0.wireOp",EDGE,"E21.2.0.4"),sQuery(id+"F0.wireOp",EDGE,"E21.2.0.5"),sQuery(id+"F0.wireOp",EDGE,"E21.2.0.6"),sQuery(id+"F0.wireOp",EDGE,"E21.2.0.7"),sQuery(id+"F0.wireOp",EDGE,"E21.2.0.9"),sQuery(id+"F0.wireOp",EDGE,"E21.2.0.10"),sQuery(id+"F0.wireOp",EDGE,"E21.2.0.13"),sQuery(id+"F0.wireOp",EDGE,"E21.2.0.14"),sQuery(id+"F0.wireOp",EDGE,"E21.2.0.17"),sQuery(id+"F0.wireOp",EDGE,"E21.2.0.18"),sQuery(id+"F0.wireOp",EDGE,"E21.2.1.2"),sQuery(id+"F0.wireOp",EDGE,"E21.2.1.3"),sQuery(id+"F0.wireOp",EDGE,"E21.2.1.4"),sQuery(id+"F0.wireOp",EDGE,"E21.2.1.5"),sQuery(id+"F0.wireOp",EDGE,"E21.2.1.6"),sQuery(id+"F0.wireOp",EDGE,"E21.2.1.7"),sQuery(id+"F0.wireOp",EDGE,"E21.2.1.9"),sQuery(id+"F0.wireOp",EDGE,"E21.2.1.10"),sQuery(id+"F0.wireOp",EDGE,"E21.2.1.13"),sQuery(id+"F0.wireOp",EDGE,"E21.2.1.14"),sQuery(id+"F0.wireOp",EDGE,"E21.2.1.17"),sQuery(id+"F0.wireOp",EDGE,"E21.2.1.18"),sQuery(id+"F0.wireOp",EDGE,"E21.2.2.2"),sQuery(id+"F0.wireOp",EDGE,"E21.2.2.3"),sQuery(id+"F0.wireOp",EDGE,"E21.2.2.4"),sQuery(id+"F0.wireOp",EDGE,"E21.2.2.5"),sQuery(id+"F0.wireOp",EDGE,"E21.2.2.6"),sQuery(id+"F0.wireOp",EDGE,"E21.2.2.7"),sQuery(id+"F0.wireOp",EDGE,"E21.2.2.9"),sQuery(id+"F0.wireOp",EDGE,"E21.2.2.10"),sQuery(id+"F0.wireOp",EDGE,"E21.2.2.13"),sQuery(id+"F0.wireOp",EDGE,"E21.2.2.14"),sQuery(id+"F0.wireOp",EDGE,"E21.2.2.17"),sQuery(id+"F0.wireOp",EDGE,"E21.2.2.18"),sQuery(id+"F0.wireOp",EDGE,"E21.2.3.2"),sQuery(id+"F0.wireOp",EDGE,"E21.2.3.3"),sQuery(id+"F0.wireOp",EDGE,"E21.2.3.4"),sQuery(id+"F0.wireOp",EDGE,"E21.2.3.5"),sQuery(id+"F0.wireOp",EDGE,"E21.2.3.6"),sQuery(id+"F0.wireOp",EDGE,"E21.2.3.7"),sQuery(id+"F0.wireOp",EDGE,"E21.2.3.9"),sQuery(id+"F0.wireOp",EDGE,"E21.2.3.10"),sQuery(id+"F0.wireOp",EDGE,"E21.2.3.13"),sQuery(id+"F0.wireOp",EDGE,"E21.2.3.14"),sQuery(id+"F0.wireOp",EDGE,"E21.2.3.17"),sQuery(id+"F0.wireOp",EDGE,"E21.2.3.18"),sQuery(id+"F0.wireOp",EDGE,"E21.3.0.2"),sQuery(id+"F0.wireOp",EDGE,"E21.3.0.3"),sQuery(id+"F0.wireOp",EDGE,"E21.3.0.4"),sQuery(id+"F0.wireOp",EDGE,"E21.3.0.5"),sQuery(id+"F0.wireOp",EDGE,"E21.3.0.6"),sQuery(id+"F0.wireOp",EDGE,"E21.3.0.7"),sQuery(id+"F0.wireOp",EDGE,"E21.3.0.9"),sQuery(id+"F0.wireOp",EDGE,"E21.3.0.10"),sQuery(id+"F0.wireOp",EDGE,"E21.3.0.13"),sQuery(id+"F0.wireOp",EDGE,"E21.3.0.14"),sQuery(id+"F0.wireOp",EDGE,"E21.3.0.17"),sQuery(id+"F0.wireOp",EDGE,"E21.3.0.18"),sQuery(id+"F0.wireOp",EDGE,"E21.3.1.2"),sQuery(id+"F0.wireOp",EDGE,"E21.3.1.3"),sQuery(id+"F0.wireOp",EDGE,"E21.3.1.4"),sQuery(id+"F0.wireOp",EDGE,"E21.3.1.5"),sQuery(id+"F0.wireOp",EDGE,"E21.3.1.6"),sQuery(id+"F0.wireOp",EDGE,"E21.3.1.7"),sQuery(id+"F0.wireOp",EDGE,"E21.3.1.9"),sQuery(id+"F0.wireOp",EDGE,"E21.3.1.10"),sQuery(id+"F0.wireOp",EDGE,"E21.3.1.13"),sQuery(id+"F0.wireOp",EDGE,"E21.3.1.14"),sQuery(id+"F0.wireOp",EDGE,"E21.3.1.17"),sQuery(id+"F0.wireOp",EDGE,"E21.3.1.18"),sQuery(id+"F0.wireOp",EDGE,"E21.3.2.2"),sQuery(id+"F0.wireOp",EDGE,"E21.3.2.3"),sQuery(id+"F0.wireOp",EDGE,"E21.3.2.4"),sQuery(id+"F0.wireOp",EDGE,"E21.3.2.5"),sQuery(id+"F0.wireOp",EDGE,"E21.3.2.6"),sQuery(id+"F0.wireOp",EDGE,"E21.3.2.7"),sQuery(id+"F0.wireOp",EDGE,"E21.3.2.9"),sQuery(id+"F0.wireOp",EDGE,"E21.3.2.10"),sQuery(id+"F0.wireOp",EDGE,"E21.3.2.13"),sQuery(id+"F0.wireOp",EDGE,"E21.3.2.14"),sQuery(id+"F0.wireOp",EDGE,"E21.3.2.17"),sQuery(id+"F0.wireOp",EDGE,"E21.3.2.18"),sQuery(id+"F0.wireOp",EDGE,"E21.3.3.2"),sQuery(id+"F0.wireOp",EDGE,"E21.3.3.3"),sQuery(id+"F0.wireOp",EDGE,"E21.3.3.4"),sQuery(id+"F0.wireOp",EDGE,"E21.3.3.5"),sQuery(id+"F0.wireOp",EDGE,"E21.3.3.6"),sQuery(id+"F0.wireOp",EDGE,"E21.3.3.7"),sQuery(id+"F0.wireOp",EDGE,"E21.3.3.9"),sQuery(id+"F0.wireOp",EDGE,"E21.3.3.10"),sQuery(id+"F0.wireOp",EDGE,"E21.3.3.13"),sQuery(id+"F0.wireOp",EDGE,"E21.3.3.14"),sQuery(id+"F0.wireOp",EDGE,"E21.3.3.17"),sQuery(id+"F0.wireOp",EDGE,"E21.3.3.18")])]});
            var Q13;
            Q13=makeQuery(id+"F2.opExtrude","SWEPT_BODY",BODY,{"disambiguationData":[OSD([sQuery(id+"F0.wireOp",EDGE,"E0.bottom"),sQuery(id+"F0.wireOp",EDGE,"E0.top"),sQuery(id+"F0.wireOp",EDGE,"E0.left"),sQuery(id+"F0.wireOp",EDGE,"E0.right"),sQuery(id+"F0.wireOp",EDGE,"E16.filletArc"),sQuery(id+"F0.wireOp",EDGE,"E17.filletArc"),sQuery(id+"F0.wireOp",EDGE,"E18.filletArc"),sQuery(id+"F0.wireOp",EDGE,"E19.filletArc"),sQuery(id+"F0.wireOp",EDGE,"E20"),sQuery(id+"F0.wireOp",EDGE,"E21.0.1.8"),sQuery(id+"F0.wireOp",EDGE,"E21.0.2.8"),sQuery(id+"F0.wireOp",EDGE,"E21.0.3.8"),sQuery(id+"F0.wireOp",EDGE,"E21.1.0.8"),sQuery(id+"F0.wireOp",EDGE,"E21.1.1.8"),sQuery(id+"F0.wireOp",EDGE,"E21.1.2.8"),sQuery(id+"F0.wireOp",EDGE,"E21.1.3.8"),sQuery(id+"F0.wireOp",EDGE,"E21.2.0.8"),sQuery(id+"F0.wireOp",EDGE,"E21.2.1.8"),sQuery(id+"F0.wireOp",EDGE,"E21.2.2.8"),sQuery(id+"F0.wireOp",EDGE,"E21.2.3.8"),sQuery(id+"F0.wireOp",EDGE,"E21.3.0.8"),sQuery(id+"F0.wireOp",EDGE,"E21.3.1.8"),sQuery(id+"F0.wireOp",EDGE,"E21.3.2.8"),sQuery(id+"F0.wireOp",EDGE,"E21.3.3.8")])]});
            hole(context, id + "F8", {"style" : HoleStyle.SIMPLE, "endStyle" : HoleEndStyle.THROUGH, "holeDiameter" : 4 * mm, "majorDiameter" : 5 * mm, "isTappedThrough" : true, "tappedDepth" : 12 * mm, "tapClearance" : 3, "locations" : qUnion([Q0, Q1, Q2, Q3, Q4, Q5, Q6, Q7, Q8, Q9, Q10, Q11]), "scope" : qUnion([Q12, Q13])});
        }
        {
            var Q0;
            Q0=sQuery(id+"F0.wireOp",VERTEX,"E18.filletArc.center");
            var Q1;
            Q1=sQuery(id+"F0.wireOp",VERTEX,"E38");
            var Q2;
            Q2=sQuery(id+"F0.wireOp",VERTEX,"E19.filletArc.center");
            var Q3;
            Q3=sQuery(id+"F0.wireOp",VERTEX,"E39");
            var Q4;
            Q4=sQuery(id+"F0.wireOp",VERTEX,"E34");
            var Q5;
            Q5=sQuery(id+"F0.wireOp",VERTEX,"E36");
            var Q6;
            Q6=sQuery(id+"F0.wireOp",VERTEX,"E37");
            var Q7;
            Q7=sQuery(id+"F0.wireOp",VERTEX,"E33");
            var Q8;
            Q8=sQuery(id+"F0.wireOp",VERTEX,"E35");
            var Q9;
            Q9=sQuery(id+"F0.wireOp",VERTEX,"E16.filletArc.center");
            var Q10;
            Q10=sQuery(id+"F0.wireOp",VERTEX,"E40");
            var Q11;
            Q11=sQuery(id+"F0.wireOp",VERTEX,"E17.filletArc.center");
            var Q12;
            Q12=makeQuery(id+"F6.opExtrude","SWEPT_BODY",BODY,{"disambiguationData":[OSD([sQuery(id+"F5.wireOp",EDGE,"E41.bottom"),sQuery(id+"F5.wireOp",EDGE,"E41.top"),sQuery(id+"F5.wireOp",EDGE,"E41.left"),sQuery(id+"F5.wireOp",EDGE,"E41.right"),sQuery(id+"F5.wireOp",EDGE,"E42.filletArc"),sQuery(id+"F5.wireOp",EDGE,"E43.filletArc"),sQuery(id+"F5.wireOp",EDGE,"E44.filletArc"),sQuery(id+"F5.wireOp",EDGE,"E45.filletArc"),sQuery(id+"F5.wireOp",EDGE,"E46"),sQuery(id+"F5.wireOp",EDGE,"E47.0.1.0"),sQuery(id+"F5.wireOp",EDGE,"E47.1.0.0"),sQuery(id+"F5.wireOp",EDGE,"E47.1.1.0"),sQuery(id+"F5.wireOp",EDGE,"E48"),sQuery(id+"F5.wireOp",EDGE,"E49"),sQuery(id+"F5.wireOp",EDGE,"E50"),sQuery(id+"F5.wireOp",EDGE,"E51"),sQuery(id+"F5.wireOp",EDGE,"E52"),sQuery(id+"F5.wireOp",EDGE,"E53"),sQuery(id+"F5.wireOp",EDGE,"E54"),sQuery(id+"F5.wireOp",EDGE,"E55"),sQuery(id+"F5.wireOp",EDGE,"E56.0.1.0"),sQuery(id+"F5.wireOp",EDGE,"E56.0.1.1"),sQuery(id+"F5.wireOp",EDGE,"E56.0.1.2"),sQuery(id+"F5.wireOp",EDGE,"E56.0.1.3"),sQuery(id+"F5.wireOp",EDGE,"E56.0.1.4"),sQuery(id+"F5.wireOp",EDGE,"E56.0.1.5"),sQuery(id+"F5.wireOp",EDGE,"E56.0.1.6"),sQuery(id+"F5.wireOp",EDGE,"E56.0.1.7"),sQuery(id+"F5.wireOp",EDGE,"E56.0.2.0"),sQuery(id+"F5.wireOp",EDGE,"E56.0.2.1"),sQuery(id+"F5.wireOp",EDGE,"E56.0.2.2"),sQuery(id+"F5.wireOp",EDGE,"E56.0.2.3"),sQuery(id+"F5.wireOp",EDGE,"E56.0.2.4"),sQuery(id+"F5.wireOp",EDGE,"E56.0.2.5"),sQuery(id+"F5.wireOp",EDGE,"E56.0.2.6"),sQuery(id+"F5.wireOp",EDGE,"E56.0.2.7"),sQuery(id+"F5.wireOp",EDGE,"E56.0.3.0"),sQuery(id+"F5.wireOp",EDGE,"E56.0.3.1"),sQuery(id+"F5.wireOp",EDGE,"E56.0.3.2"),sQuery(id+"F5.wireOp",EDGE,"E56.0.3.3"),sQuery(id+"F5.wireOp",EDGE,"E56.0.3.4"),sQuery(id+"F5.wireOp",EDGE,"E56.0.3.5"),sQuery(id+"F5.wireOp",EDGE,"E56.0.3.6"),sQuery(id+"F5.wireOp",EDGE,"E56.0.3.7"),sQuery(id+"F5.wireOp",EDGE,"E56.1.0.0"),sQuery(id+"F5.wireOp",EDGE,"E56.1.0.1"),sQuery(id+"F5.wireOp",EDGE,"E56.1.0.2"),sQuery(id+"F5.wireOp",EDGE,"E56.1.0.3"),sQuery(id+"F5.wireOp",EDGE,"E56.1.0.4"),sQuery(id+"F5.wireOp",EDGE,"E56.1.0.5"),sQuery(id+"F5.wireOp",EDGE,"E56.1.0.6"),sQuery(id+"F5.wireOp",EDGE,"E56.1.0.7"),sQuery(id+"F5.wireOp",EDGE,"E56.1.1.0"),sQuery(id+"F5.wireOp",EDGE,"E56.1.1.1"),sQuery(id+"F5.wireOp",EDGE,"E56.1.1.2"),sQuery(id+"F5.wireOp",EDGE,"E56.1.1.3"),sQuery(id+"F5.wireOp",EDGE,"E56.1.1.4"),sQuery(id+"F5.wireOp",EDGE,"E56.1.1.5"),sQuery(id+"F5.wireOp",EDGE,"E56.1.1.6"),sQuery(id+"F5.wireOp",EDGE,"E56.1.1.7"),sQuery(id+"F5.wireOp",EDGE,"E56.1.2.0"),sQuery(id+"F5.wireOp",EDGE,"E56.1.2.1"),sQuery(id+"F5.wireOp",EDGE,"E56.1.2.2"),sQuery(id+"F5.wireOp",EDGE,"E56.1.2.3"),sQuery(id+"F5.wireOp",EDGE,"E56.1.2.4"),sQuery(id+"F5.wireOp",EDGE,"E56.1.2.5"),sQuery(id+"F5.wireOp",EDGE,"E56.1.2.6"),sQuery(id+"F5.wireOp",EDGE,"E56.1.2.7"),sQuery(id+"F5.wireOp",EDGE,"E56.1.3.0"),sQuery(id+"F5.wireOp",EDGE,"E56.1.3.1"),sQuery(id+"F5.wireOp",EDGE,"E56.1.3.2"),sQuery(id+"F5.wireOp",EDGE,"E56.1.3.3"),sQuery(id+"F5.wireOp",EDGE,"E56.1.3.4"),sQuery(id+"F5.wireOp",EDGE,"E56.1.3.5"),sQuery(id+"F5.wireOp",EDGE,"E56.1.3.6"),sQuery(id+"F5.wireOp",EDGE,"E56.1.3.7"),sQuery(id+"F5.wireOp",EDGE,"E56.2.0.0"),sQuery(id+"F5.wireOp",EDGE,"E56.2.0.1"),sQuery(id+"F5.wireOp",EDGE,"E56.2.0.2"),sQuery(id+"F5.wireOp",EDGE,"E56.2.0.3"),sQuery(id+"F5.wireOp",EDGE,"E56.2.0.4"),sQuery(id+"F5.wireOp",EDGE,"E56.2.0.5"),sQuery(id+"F5.wireOp",EDGE,"E56.2.0.6"),sQuery(id+"F5.wireOp",EDGE,"E56.2.0.7"),sQuery(id+"F5.wireOp",EDGE,"E56.2.1.0"),sQuery(id+"F5.wireOp",EDGE,"E56.2.1.1"),sQuery(id+"F5.wireOp",EDGE,"E56.2.1.2"),sQuery(id+"F5.wireOp",EDGE,"E56.2.1.3"),sQuery(id+"F5.wireOp",EDGE,"E56.2.1.4"),sQuery(id+"F5.wireOp",EDGE,"E56.2.1.5"),sQuery(id+"F5.wireOp",EDGE,"E56.2.1.6"),sQuery(id+"F5.wireOp",EDGE,"E56.2.1.7"),sQuery(id+"F5.wireOp",EDGE,"E56.2.2.0"),sQuery(id+"F5.wireOp",EDGE,"E56.2.2.1"),sQuery(id+"F5.wireOp",EDGE,"E56.2.2.2"),sQuery(id+"F5.wireOp",EDGE,"E56.2.2.3"),sQuery(id+"F5.wireOp",EDGE,"E56.2.2.4"),sQuery(id+"F5.wireOp",EDGE,"E56.2.2.5"),sQuery(id+"F5.wireOp",EDGE,"E56.2.2.6"),sQuery(id+"F5.wireOp",EDGE,"E56.2.2.7"),sQuery(id+"F5.wireOp",EDGE,"E56.2.3.0"),sQuery(id+"F5.wireOp",EDGE,"E56.2.3.1"),sQuery(id+"F5.wireOp",EDGE,"E56.2.3.2"),sQuery(id+"F5.wireOp",EDGE,"E56.2.3.3"),sQuery(id+"F5.wireOp",EDGE,"E56.2.3.4"),sQuery(id+"F5.wireOp",EDGE,"E56.2.3.5"),sQuery(id+"F5.wireOp",EDGE,"E56.2.3.6"),sQuery(id+"F5.wireOp",EDGE,"E56.2.3.7"),sQuery(id+"F5.wireOp",EDGE,"E56.3.0.0"),sQuery(id+"F5.wireOp",EDGE,"E56.3.0.1"),sQuery(id+"F5.wireOp",EDGE,"E56.3.0.2"),sQuery(id+"F5.wireOp",EDGE,"E56.3.0.3"),sQuery(id+"F5.wireOp",EDGE,"E56.3.0.4"),sQuery(id+"F5.wireOp",EDGE,"E56.3.0.5"),sQuery(id+"F5.wireOp",EDGE,"E56.3.0.6"),sQuery(id+"F5.wireOp",EDGE,"E56.3.0.7"),sQuery(id+"F5.wireOp",EDGE,"E56.3.1.0"),sQuery(id+"F5.wireOp",EDGE,"E56.3.1.1"),sQuery(id+"F5.wireOp",EDGE,"E56.3.1.2"),sQuery(id+"F5.wireOp",EDGE,"E56.3.1.3"),sQuery(id+"F5.wireOp",EDGE,"E56.3.1.4"),sQuery(id+"F5.wireOp",EDGE,"E56.3.1.5"),sQuery(id+"F5.wireOp",EDGE,"E56.3.1.6"),sQuery(id+"F5.wireOp",EDGE,"E56.3.1.7"),sQuery(id+"F5.wireOp",EDGE,"E56.3.2.0"),sQuery(id+"F5.wireOp",EDGE,"E56.3.2.1"),sQuery(id+"F5.wireOp",EDGE,"E56.3.2.2"),sQuery(id+"F5.wireOp",EDGE,"E56.3.2.3"),sQuery(id+"F5.wireOp",EDGE,"E56.3.2.4"),sQuery(id+"F5.wireOp",EDGE,"E56.3.2.5"),sQuery(id+"F5.wireOp",EDGE,"E56.3.2.6"),sQuery(id+"F5.wireOp",EDGE,"E56.3.2.7"),sQuery(id+"F5.wireOp",EDGE,"E56.3.3.0"),sQuery(id+"F5.wireOp",EDGE,"E56.3.3.1"),sQuery(id+"F5.wireOp",EDGE,"E56.3.3.2"),sQuery(id+"F5.wireOp",EDGE,"E56.3.3.3"),sQuery(id+"F5.wireOp",EDGE,"E56.3.3.4"),sQuery(id+"F5.wireOp",EDGE,"E56.3.3.5"),sQuery(id+"F5.wireOp",EDGE,"E56.3.3.6"),sQuery(id+"F5.wireOp",EDGE,"E56.3.3.7")])]});
            hole(context, id + "F9", {"style" : HoleStyle.SIMPLE, "endStyle" : HoleEndStyle.THROUGH, "oppositeDirection" : true, "holeDiameter" : 4 * mm, "majorDiameter" : 5 * mm, "isTappedThrough" : true, "tappedDepth" : 12 * mm, "tapClearance" : 3, "locations" : qUnion([Q0, Q1, Q2, Q3, Q4, Q5, Q6, Q7, Q8, Q9, Q10, Q11]), "scope" : qUnion([Q12])});
        }
    });
